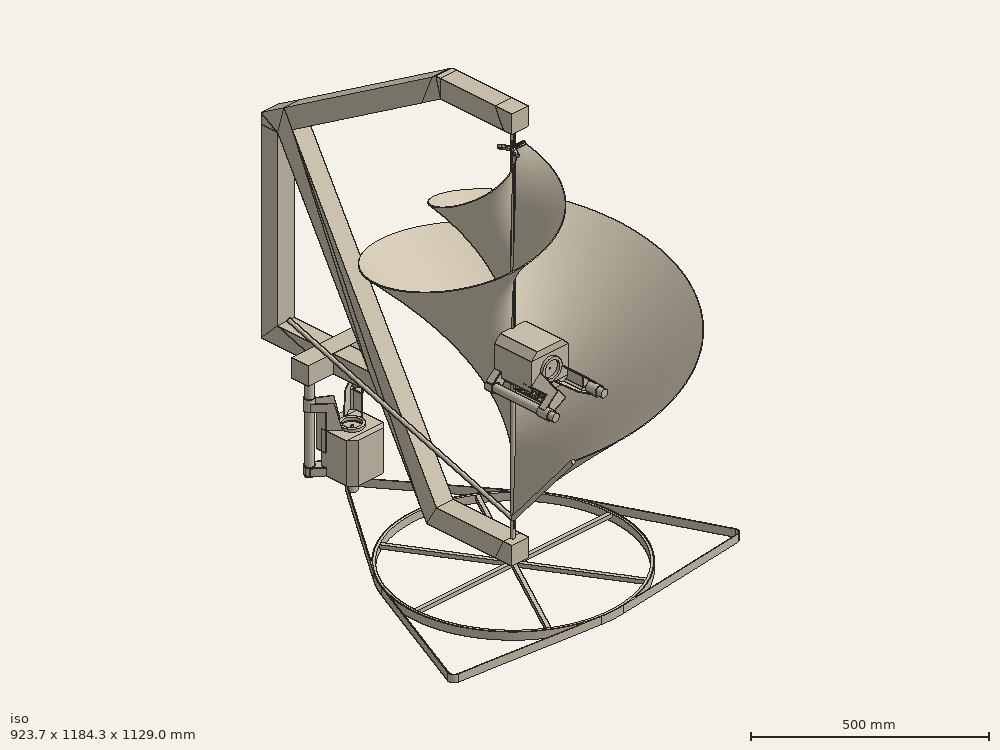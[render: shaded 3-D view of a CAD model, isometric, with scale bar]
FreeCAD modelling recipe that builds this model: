
FCSTD DOCUMENT  (FreeCAD 0.20R29410 (Git))
Label: BASE Con motor
License: All rights reserved
LicenseURL: http://en.wikipedia.org/wiki/All_rights_reserved
objects: Part::Part2DObjectPython×90, Part::Extrusion×53, Part::RuledSurface×40, Sketcher::SketchObject×21, Part::MultiFuse×12, Part::Face×9, Mesh::Feature×9, App::Link×7, Part::FeaturePython×6, App::LinkGroup×5, Part::Feature×5, Part::Cut×4, Part::MultiCommon×4, Part::Cylinder×3, Part::Sweep×2, Part::Helix×1, Part::Offset×1, Part::Fillet×1, App::DocumentObjectGroup×1, Part::Box×1
note: 253 computed .brp shape members not serialized (recipe doc carries the construction recipe); baked Part::Feature solids carry a one-line shape summary decoded from their .brp

FEATURE [Part::Helix] Helix  label="Hélice"
  Angle = -43
  AttacherType = Attacher::AttachEngine3D
  Height = 490
  LocalCoord = 0
  Pitch = 490
  Radius = 490
  SegmentLength = 0
  Style = 1
FEATURE [Sketcher::SketchObject] Sketch001
  ExternalGeometry = -> [Helix]
  FullyConstrained = true
  Placement = pos=(0,0,0) rot=(1,0,0;1.5708rad)
  sketch-geometry (4):
    g0: LineSegment StartX=0 StartY=490 StartZ=0 EndX=0 EndY=-411.159 EndZ=0
    g1: LineSegment StartX=490 StartY=0 StartZ=0 EndX=0 EndY=-411.159 EndZ=0
    g2: LineSegment StartX=490 StartY=0 StartZ=0 EndX=0 EndY=-411.159 EndZ=0
    g3: Circle CenterX=490 CenterY=0 CenterZ=0 NormalX=0 NormalY=0 NormalZ=1 AngleXU=0 Radius=5
  constraints (10):
    c: PointOnObject(g0,g-2)
    c: Horizontal(g0,g-3)
    c: Vertical(g0)
    c: Coincident(g1,g-4)
    c: Coincident(g1,g0)
    c: Angle(g1,g0) = 0.872665
    c: Coincident(g2,g1)
    c: Coincident(g2,g0)
    c: Coincident(g3,g2)
    c: Diameter(g3) = 10
FEATURE [Part::RuledSurface] Ruled_Surface
  Curve1 = -> Sketch001 [Edge1]
  Curve2 = -> Helix [Edge1]
  Orientation = 0
FEATURE [Part::Offset] Offset
  Fill = true
  Intersection = false
  Join = 0
  Mode = 0
  SelfIntersection = false
  Source = -> Ruled_Surface
  Value = 2
FEATURE [Part::Fillet] Fillet
  Base = -> Offset
  Edges = 1 edges r=1: [Edge8]
FEATURE [Sketcher::SketchObject] Sketch
  ExternalGeometry = -> [Helix]
  FullyConstrained = true
  MapMode = 2
  sketch-geometry (2):
    g0: Circle CenterX=0 CenterY=0 CenterZ=0 NormalX=0 NormalY=0 NormalZ=1 AngleXU=0 Radius=5
    g1: LineSegment StartX=33.0676 StartY=0 StartZ=0 EndX=0 EndY=0 EndZ=0
  constraints (4):
    c: Coincident(g0,g-1)
    c: Diameter(g0) = 10
    c: Coincident(g1,g-3)
    c: Coincident(g1,g0)
FEATURE [Sketcher::SketchObject] Sketch002
  ExternalGeometry = -> [Helix]
  FullyConstrained = true
  Placement = pos=(0,0,0) rot=(0.57735,0.57735,0.57735;2.0944rad)
  sketch-geometry (1):
    g0: Circle CenterX=0 CenterY=490 CenterZ=0 NormalX=0 NormalY=0 NormalZ=1 AngleXU=0 Radius=5
  constraints (2):
    c: Coincident(g0,g-3)
    c: Diameter(g0) = 10
FEATURE [Part::Cylinder] Cylinder  label="Cilindro"
  Angle = 360
  AttacherType = Attacher::AttachEngine3D
  FirstAngle = 0
  Height = 640
  Placement = pos=(0,0,-411.16) rot=(0,1,0;0.872665rad)
  Radius = 5
  SecondAngle = 0
FEATURE [Sketcher::SketchObject] Sketch003
  FullyConstrained = true
  sketch-geometry (1):
    g0: Circle CenterX=0 CenterY=0 CenterZ=0 NormalX=0 NormalY=0 NormalZ=1 AngleXU=0 Radius=5
  constraints (2):
    c: Coincident(g0,g-1)
    c: Diameter(g0) = 10
FEATURE [Sketcher::SketchObject] Sketch004
  ExternalGeometry = -> [Helix,Sketch001]
  FullyConstrained = true
  Placement = pos=(0,0,0) rot=(1,0,0;1.5708rad)
  sketch-geometry (1):
    g0: LineSegment StartX=0 StartY=539.42 StartZ=0 EndX=0 EndY=-460.579 EndZ=0
  constraints (4):
    c: Vertical(g0)
    c: DistanceY(g-3,g0) = 49.42
    c: DistanceY(g0,g-4) = 49.42
    c: Vertical(g0,g-4)
FEATURE [Part::Sweep] Sweep
  Frenet = false
  Sections = -> [Sketch003]
  Solid = true
  Spine = -> Sketch004 [Edge1]
  Transition = 1
FEATURE [Part::Sweep] Sweep001
  Frenet = false
  Sections = -> [Sketch002]
  Solid = true
  Spine = -> Sketch [Edge2]
  Transition = 1
FEATURE [Sketcher::SketchObject] Sketch005
  ExternalGeometry = -> [Helix]
  FullyConstrained = true
  Placement = pos=(0,0,0) rot=(1,0,0;1.5708rad)
  sketch-geometry (1):
    g0: Circle CenterX=490 CenterY=0 CenterZ=0 NormalX=0 NormalY=0 NormalZ=1 AngleXU=0 Radius=5
  constraints (2):
    c: Coincident(g0,g-3)
    c: Diameter(g0) = 10
FEATURE [Part::Part2DObjectPython] Line007  # Draft 2D object (typed FeaturePython)
  Area = 0
  ChamferSize = 0
  Closed = false
  End = (3e-14,3855,-1010.3)
  FilletRadius = 0
  Length = 45.7
  MakeFace = true
  Placement = pos=(2.7e-14,3855,-1056) rot=(0.57735,0.57735,0.57735;2.0944rad)
  Points = (2) [(0,0,0),(0,45.7,2.79832e-15)]
  Start = (2.72e-14,3855,-1056)
  Subdivisions = 0
FEATURE [Part::Part2DObjectPython] Line010  # Draft 2D object (typed FeaturePython)
  Area = 0
  ChamferSize = 0
  Closed = false
  End = (8.8e-14,3855,-101.7)
  FilletRadius = 0
  Length = 45.7
  MakeFace = true
  Placement = pos=(8.8e-14,3855,-56) rot=(0.57735,0.57735,0.57735;2.0944rad)
  Points = (2) [(0,0,0),(0,-45.7,0)]
  Start = (8.8e-14,3855,-56)
  Subdivisions = 0
FEATURE [Part::Part2DObjectPython] Line019  # Draft 2D object (typed FeaturePython)
  Area = 0
  ChamferSize = 0
  Closed = false
  End = (5.71e-14,4300,-568.3)
  FilletRadius = 0
  Length = 890
  MakeFace = true
  Placement = pos=(5.7e-14,3410,-568.3) rot=(0.57735,0.57735,0.57735;2.0944rad)
  Points = (2) [(0,0,0),(890,0,0)]
  Start = (5.71e-14,3410,-568.3)
  Subdivisions = 0
FEATURE [Part::Part2DObjectPython] Line020  # Draft 2D object (typed FeaturePython)
  Area = 0
  ChamferSize = 0
  Closed = false
  End = (3e-14,3855,-1010.3)
  FilletRadius = 0
  Length = 627.207
  MakeFace = true
  Placement = pos=(5.7e-14,3410,-568.3) rot=(0.57735,0.57735,0.57735;2.0944rad)
  Points = (2) [(0,0,0),(445,-442,-2.70647e-14)]
  Start = (5.71e-14,3410,-568.3)
  Subdivisions = 0
FEATURE [Part::Part2DObjectPython] Line021  # Draft 2D object (typed FeaturePython)
  Area = 0
  ChamferSize = 0
  Closed = false
  End = (3e-14,3855,-1010.3)
  FilletRadius = 0
  Length = 627.207
  MakeFace = true
  Placement = pos=(5.7e-14,4300,-568.3) rot=(0.57735,0.57735,0.57735;2.0944rad)
  Points = (2) [(0,0,0),(-445,-442,-2.70647e-14)]
  Start = (5.71e-14,4300,-568.3)
  Subdivisions = 0
FEATURE [Part::Part2DObjectPython] Line028  # Draft 2D object (typed FeaturePython)
  Area = 0
  ChamferSize = 0
  Closed = false
  End = (0,4125,-311)
  FilletRadius = 0
  Length = 270
  MakeFace = true
  Placement = pos=(0,3855,-311) rot=(0.57735,0.57735,0.57735;2.0944rad)
  Points = (2) [(0,0,0),(270,0,0)]
  Start = (0,3855,-311)
  Subdivisions = 0
FEATURE [Part::Part2DObjectPython] Line029  # Draft 2D object (typed FeaturePython)
  Area = 0
  ChamferSize = 0
  Closed = false
  End = (0,3585,-311)
  FilletRadius = 0
  Length = 270
  MakeFace = true
  Placement = pos=(0,3855,-311) rot=(0.57735,0.57735,0.57735;2.0944rad)
  Points = (2) [(0,0,0),(-270,0,0)]
  Start = (0,3855,-311)
  Subdivisions = 0
FEATURE [Part::Part2DObjectPython] Line030  # Draft 2D object (typed FeaturePython)
  Area = 0
  ChamferSize = 0
  Closed = false
  End = (5.71e-14,3855,-568.3)
  FilletRadius = 0
  Length = 372.966
  MakeFace = true
  Placement = pos=(0,3585,-311) rot=(0.57735,0.57735,0.57735;2.0944rad)
  Points = (2) [(0,0,0),(270,-257.3,5.71114e-14)]
  Start = (0,3585,-311)
  Subdivisions = 0
FEATURE [Part::Part2DObjectPython] Line031  # Draft 2D object (typed FeaturePython)
  Area = 0
  ChamferSize = 0
  Closed = false
  End = (5.71e-14,3855,-568.3)
  FilletRadius = 0
  Length = 372.966
  MakeFace = true
  Placement = pos=(0,4125,-311) rot=(0.57735,0.57735,0.57735;2.0944rad)
  Points = (2) [(0,0,0),(-270,-257.3,5.71114e-14)]
  Start = (0,4125,-311)
  Subdivisions = 0
FEATURE [Part::Part2DObjectPython] Line032  # Draft 2D object (typed FeaturePython)
  Area = 0
  ChamferSize = 0
  Closed = false
  End = (8.8e-14,3735,-101.7)
  FilletRadius = 0
  Length = 120
  MakeFace = true
  Placement = pos=(8.8e-14,3855,-101.7) rot=(0.57735,0.57735,0.57735;2.0944rad)
  Points = (2) [(0,0,0),(-120,0,0)]
  Start = (8.8e-14,3855,-101.7)
  Subdivisions = 0
FEATURE [Part::Part2DObjectPython] Line033  # Draft 2D object (typed FeaturePython)
  Area = 0
  ChamferSize = 0
  Closed = false
  End = (-5e-16,3855,-311.004)
  FilletRadius = 0
  Length = 241.264
  MakeFace = true
  Placement = pos=(8.8e-14,3735,-101.7) rot=(0.57735,0.57735,0.57735;2.0944rad)
  Points = (2) [(0,0,0),(120.002,-209.304,-8.84807e-14)]
  Start = (8.8e-14,3735,-101.7)
  Subdivisions = 0
FEATURE [Part::Part2DObjectPython] Line034  # Draft 2D object (typed FeaturePython)
  Area = 0
  ChamferSize = 0
  Closed = false
  End = (8.8e-14,3975,-101.7)
  FilletRadius = 0
  Length = 120
  MakeFace = true
  Placement = pos=(8.8e-14,3855,-101.7) rot=(0.57735,0.57735,0.57735;2.0944rad)
  Points = (2) [(0,0,0),(120,0,0)]
  Start = (8.8e-14,3855,-101.7)
  Subdivisions = 0
FEATURE [Part::Part2DObjectPython] Line035  # Draft 2D object (typed FeaturePython)
  Area = 0
  ChamferSize = 0
  Closed = false
  End = (-5e-16,3855,-311)
  FilletRadius = 0
  Length = 241.26
  MakeFace = true
  Placement = pos=(8.8e-14,3975,-101.7) rot=(0.57735,0.57735,0.57735;2.0944rad)
  Points = (2) [(0,0,0),(-120,-209.3,-8.84807e-14)]
  Start = (8.8e-14,3975,-101.7)
  Subdivisions = 0
FEATURE [Part::Part2DObjectPython] Line036  # Draft 2D object (typed FeaturePython)
  Area = 0
  ChamferSize = 0
  Closed = false
  End = (2.72e-14,3915,-1056)
  FilletRadius = 0
  Length = 60
  MakeFace = true
  Placement = pos=(2.7e-14,3855,-1056) rot=(0.57735,0.57735,0.57735;2.0944rad)
  Points = (2) [(0,0,0),(60,0,0)]
  Start = (2.72e-14,3855,-1056)
  Subdivisions = 0
FEATURE [Part::Part2DObjectPython] Line037  # Draft 2D object (typed FeaturePython)
  Area = 0
  ChamferSize = 0
  Closed = false
  End = (2.72e-14,3795,-1056)
  FilletRadius = 0
  Length = 60
  MakeFace = true
  Placement = pos=(2.7e-14,3855,-1056) rot=(0.57735,0.57735,0.57735;2.0944rad)
  Points = (2) [(0,0,0),(-60,0,0)]
  Start = (2.72e-14,3855,-1056)
  Subdivisions = 0
FEATURE [Part::Part2DObjectPython] Line038  # Draft 2D object (typed FeaturePython)
  Area = 0
  ChamferSize = 0
  Closed = false
  End = (2.72e-14,3795,-1176)
  FilletRadius = 0
  Length = 120
  MakeFace = true
  Placement = pos=(2.7e-14,3795,-1056) rot=(0.57735,0.57735,0.57735;2.0944rad)
  Points = (2) [(0,0,0),(0,-120,0)]
  Start = (2.72e-14,3795,-1056)
  Subdivisions = 0
FEATURE [Part::Part2DObjectPython] Line039  # Draft 2D object (typed FeaturePython)
  Area = 0
  ChamferSize = 0
  Closed = false
  End = (2.72e-14,4155,-1176)
  FilletRadius = 0
  Length = 360
  MakeFace = true
  Placement = pos=(2.7e-14,3795,-1176) rot=(0.57735,0.57735,0.57735;2.0944rad)
  Points = (2) [(0,0,0),(360,0,0)]
  Start = (2.72e-14,3795,-1176)
  Subdivisions = 0
FEATURE [Part::Part2DObjectPython] Line040  # Draft 2D object (typed FeaturePython)
  Area = 0
  ChamferSize = 0
  Closed = false
  End = (2.72e-14,4155,-1056)
  FilletRadius = 0
  Length = 240
  MakeFace = true
  Placement = pos=(2.7e-14,3915,-1056) rot=(0.57735,0.57735,0.57735;2.0944rad)
  Points = (2) [(0,0,0),(240,0,0)]
  Start = (2.72e-14,3915,-1056)
  Subdivisions = 0
FEATURE [Part::Part2DObjectPython] Line041  # Draft 2D object (typed FeaturePython)
  Area = 0
  ChamferSize = 0
  Closed = false
  End = (8.8e-14,3795,-56)
  FilletRadius = 0
  Length = 60
  MakeFace = true
  Placement = pos=(8.8e-14,3855,-56) rot=(0.57735,0.57735,0.57735;2.0944rad)
  Points = (2) [(0,0,0),(-60,0,0)]
  Start = (8.8e-14,3855,-56)
  Subdivisions = 0
FEATURE [Part::Part2DObjectPython] Line042  # Draft 2D object (typed FeaturePython)
  Area = 0
  ChamferSize = 0
  Closed = false
  End = (8.8e-14,3795,64)
  FilletRadius = 0
  Length = 120
  MakeFace = true
  Placement = pos=(8.8e-14,3795,-56) rot=(0.57735,0.57735,0.57735;2.0944rad)
  Points = (2) [(0,0,0),(0,120,0)]
  Start = (8.8e-14,3795,-56)
  Subdivisions = 0
FEATURE [Part::Part2DObjectPython] Line043  # Draft 2D object (typed FeaturePython)
  Area = 0
  ChamferSize = 0
  Closed = false
  End = (8.8e-14,3915,64)
  FilletRadius = 0
  Length = 120
  MakeFace = true
  Placement = pos=(8.8e-14,3795,64) rot=(0.57735,0.57735,0.57735;2.0944rad)
  Points = (2) [(0,0,0),(120,0,0)]
  Start = (8.8e-14,3795,64)
  Subdivisions = 0
FEATURE [Part::Part2DObjectPython] Line045  # Draft 2D object (typed FeaturePython)
  Area = 0
  ChamferSize = 0
  Closed = false
  End = (8.8e-14,3855,-56)
  FilletRadius = 0
  Length = 60
  MakeFace = true
  Placement = pos=(8.8e-14,3915,-56) rot=(0.57735,0.57735,0.57735;2.0944rad)
  Points = (2) [(0,0,0),(-60,0,0)]
  Start = (8.8e-14,3915,-56)
  Subdivisions = 0
FEATURE [Part::Part2DObjectPython] Line048  # Draft 2D object (typed FeaturePython)
  Area = 0
  ChamferSize = 0
  Closed = false
  End = (8.8e-14,3855,184)
  FilletRadius = 0
  Length = 15
  MakeFace = true
  Placement = pos=(8.8e-14,3840,184) rot=(0.57735,0.57735,0.57735;2.0944rad)
  Points = (2) [(0,0,0),(15,0,0)]
  Start = (8.8e-14,3840,184)
  Subdivisions = 0
FEATURE [Part::Part2DObjectPython] Line049  # Draft 2D object (typed FeaturePython)
  Area = 0
  ChamferSize = 0
  Closed = false
  End = (8.8e-14,3870,184)
  FilletRadius = 0
  Length = 15
  MakeFace = true
  Placement = pos=(8.8e-14,3855,184) rot=(0.57735,0.57735,0.57735;2.0944rad)
  Points = (2) [(0,0,0),(15,0,0)]
  Start = (8.8e-14,3855,184)
  Subdivisions = 0
FEATURE [Part::Part2DObjectPython] Line052  # Draft 2D object (typed FeaturePython)
  Area = 0
  ChamferSize = 0
  Closed = false
  End = (8.8e-14,3840,184)
  FilletRadius = 0
  Length = 128.16
  MakeFace = true
  Placement = pos=(8.8e-14,3795,64) rot=(0.57735,0.57735,0.57735;2.0944rad)
  Points = (2) [(0,0,0),(45,120,0)]
  Start = (8.8e-14,3795,64)
  Subdivisions = 0
FEATURE [Part::Part2DObjectPython] Line053  # Draft 2D object (typed FeaturePython)
  Area = 0
  ChamferSize = 0
  Closed = false
  End = (8.8e-14,3915,64)
  FilletRadius = 0
  Length = 128.16
  MakeFace = true
  Placement = pos=(8.8e-14,3870,184) rot=(0.57735,0.57735,0.57735;2.0944rad)
  Points = (2) [(0,0,0),(45,-120,0)]
  Start = (8.8e-14,3870,184)
  Subdivisions = 0
FEATURE [Part::Part2DObjectPython] Line056  # Draft 2D object (typed FeaturePython)
  Area = 0
  ChamferSize = 0
  Closed = false
  End = (8.8e-14,4035,-56)
  FilletRadius = 0
  Length = 120
  MakeFace = true
  Placement = pos=(8.8e-14,3915,-56) rot=(0.57735,0.57735,0.57735;2.0944rad)
  Points = (2) [(0,0,0),(120,0,0)]
  Start = (8.8e-14,3915,-56)
  Subdivisions = 0
FEATURE [Part::Part2DObjectPython] Line065  # Draft 2D object (typed FeaturePython)
  Area = 0
  ChamferSize = 0
  Closed = false
  End = (2.72e-14,4239.02,-1176)
  FilletRadius = 0
  Length = 82.7215
  MakeFace = true
  Placement = pos=(2.7e-14,4156.3,-1176) rot=(0.57735,0.57735,0.57735;2.0944rad)
  Points = (2) [(0,0,0),(82.7215,0,0)]
  Start = (2.72e-14,4156.3,-1176)
  Subdivisions = 0
FEATURE [Part::Part2DObjectPython] Line067  # Draft 2D object (typed FeaturePython)
  Area = 0
  ChamferSize = 0
  Closed = false
  End = (8.8e-14,4036.92,64)
  FilletRadius = 0
  Length = 120
  MakeFace = true
  Placement = pos=(8.8e-14,3916.92,64) rot=(0.57735,0.57735,0.57735;2.0944rad)
  Points = (2) [(0,0,0),(120,0,0)]
  Start = (8.8e-14,3916.92,64)
  Subdivisions = 0
FEATURE [Part::Part2DObjectPython] Line074  # Draft 2D object (typed FeaturePython)
  Area = 0
  ChamferSize = 0
  Closed = false
  End = (2.75e-14,4239.02,-1176)
  FilletRadius = 0
  Length = 262.016
  MakeFace = true
  Placement = pos=(5.2e-14,4328.64,-929.785) rot=(0.57735,0.57735,0.57735;2.0944rad)
  Points = (2) [(0,0,0),(-89.6141,-246.215,-2.44929e-14)]
  Start = (5.2e-14,4328.64,-929.785)
  Subdivisions = 0
FEATURE [Part::Part2DObjectPython] Line080  # Draft 2D object (typed FeaturePython)
  Area = 0
  ChamferSize = 0
  Closed = false
  End = (6.12e-14,4478.64,-929.785)
  FilletRadius = 0
  Length = 150
  MakeFace = true
  Placement = pos=(5.2e-14,4328.64,-929.785) rot=(0.57735,0.57735,0.57735;2.0944rad)
  Points = (2) [(0,0,0),(150,0,9.18485e-15)]
  Start = (5.2e-14,4328.64,-929.785)
  Subdivisions = 0
FEATURE [Part::Part2DObjectPython] Line081  # Draft 2D object (typed FeaturePython)
  Area = 0
  ChamferSize = 0
  Closed = false
  End = (6.09e-14,4478.64,-1176)
  FilletRadius = 0
  Length = 246.215
  MakeFace = true
  Placement = pos=(6.1e-14,4478.64,-929.785) rot=(0.57735,0.57735,0.57735;2.0944rad)
  Points = (2) [(0,0,0),(0,-246.215,0)]
  Start = (6.09e-14,4478.64,-929.785)
  Subdivisions = 0
FEATURE [Part::Part2DObjectPython] Line083  # Draft 2D object (typed FeaturePython)
  Area = 0
  ChamferSize = 0
  Closed = false
  End = (6.09e-14,4529.68,-1176)
  FilletRadius = 0
  Length = 51.04
  MakeFace = true
  Placement = pos=(6.1e-14,4478.64,-1176) rot=(0.57735,0.57735,0.57735;2.0944rad)
  Points = (2) [(0,0,0),(51.04,0,0)]
  Start = (6.09e-14,4478.64,-1176)
  Subdivisions = 0
FEATURE [Part::Part2DObjectPython] Line084  # Draft 2D object (typed FeaturePython)
  Area = 0
  ChamferSize = 0
  Closed = false
  End = (6.09e-14,4529.68,-929.785)
  FilletRadius = 0
  Length = 246.215
  MakeFace = true
  Placement = pos=(6.1e-14,4529.68,-1176) rot=(0.57735,0.57735,0.57735;2.0944rad)
  Points = (2) [(0,0,0),(0,246.215,0)]
  Start = (6.09e-14,4529.68,-1176)
  Subdivisions = 0
FEATURE [Part::Part2DObjectPython] Line085  # Draft 2D object (typed FeaturePython)
  Area = 0
  ChamferSize = 0
  Closed = false
  End = (7.01e-14,4679.68,-929.785)
  FilletRadius = 0
  Length = 150
  MakeFace = true
  Placement = pos=(6.1e-14,4529.68,-929.785) rot=(0.57735,0.57735,0.57735;2.0944rad)
  Points = (2) [(0,0,0),(150,0,9.18485e-15)]
  Start = (6.09e-14,4529.68,-929.785)
  Subdivisions = 0
FEATURE [Part::Part2DObjectPython] Line086  # Draft 2D object (typed FeaturePython)
  Area = 0
  ChamferSize = 0
  Closed = false
  End = (7.01e-14,4679.68,-570.81)
  FilletRadius = 0
  Length = 358.975
  MakeFace = true
  Placement = pos=(7e-14,4679.68,-929.785) rot=(0.57735,0.57735,0.57735;2.0944rad)
  Points = (2) [(0,0,0),(0,358.975,0)]
  Start = (7.01e-14,4679.68,-929.785)
  Subdivisions = 0
FEATURE [Part::Part2DObjectPython] Line088  # Draft 2D object (typed FeaturePython)
  Area = 0
  ChamferSize = 0
  Closed = false
  End = (5.2e-14,4559.68,-817.025)
  FilletRadius = 0
  Length = 190
  MakeFace = true
  Placement = pos=(5.2e-14,4369.68,-817.025) rot=(0.57735,0.57735,0.57735;2.0944rad)
  Points = (2) [(0,0,0),(190,0,0)]
  Start = (5.2e-14,4369.68,-817.025)
  Subdivisions = 0
FEATURE [Part::Part2DObjectPython] Line091  # Draft 2D object (typed FeaturePython)
  Area = 0
  ChamferSize = 0
  Closed = false
  End = (7.01e-14,4679.68,-450.81)
  FilletRadius = 0
  Length = 120
  MakeFace = true
  Placement = pos=(7e-14,4679.68,-570.81) rot=(0.57735,0.57735,0.57735;2.0944rad)
  Points = (2) [(0,0,0),(0,120,0)]
  Start = (7.01e-14,4679.68,-570.81)
  Subdivisions = 0
FEATURE [Part::Part2DObjectPython] Line096  # Draft 2D object (typed FeaturePython)
  Area = 0
  ChamferSize = 0
  Closed = false
  End = (8.8e-14,4066.16,64)
  FilletRadius = 0
  Length = 29.2349
  MakeFace = true
  Placement = pos=(8.8e-14,4036.92,64) rot=(0.57735,0.57735,0.57735;2.0944rad)
  Points = (2) [(0,0,0),(29.2349,0,0)]
  Start = (8.8e-14,4036.92,64)
  Subdivisions = 0
FEATURE [Part::Part2DObjectPython] Line101  # Draft 2D object (typed FeaturePython)
  Area = 0
  ChamferSize = 0
  Closed = false
  End = (7.01e-14,4679.68,-304.25)
  FilletRadius = 0
  Length = 146.56
  MakeFace = true
  Placement = pos=(7e-14,4679.68,-450.81) rot=(0.57735,0.57735,0.57735;2.0944rad)
  Points = (2) [(0,0,0),(0,146.56,0)]
  Start = (7.01e-14,4679.68,-450.81)
  Subdivisions = 0
FEATURE [Part::Part2DObjectPython] Line102  # Draft 2D object (typed FeaturePython)
  Area = 0
  ChamferSize = 0
  Closed = false
  End = (7.75e-14,4437.17,-280.75)
  FilletRadius = 0
  Length = 825.005
  MakeFace = true
  Placement = pos=(2.7e-14,4155,-1056) rot=(0.57735,0.57735,0.57735;2.0944rad)
  Points = (2) [(0,0,0),(282.17,775.25,5.05167e-14)]
  Start = (2.72e-14,4155,-1056)
  Subdivisions = 0
FEATURE [Part::Part2DObjectPython] Line103  # Draft 2D object (typed FeaturePython)
  Area = 0
  ChamferSize = 0
  Closed = false
  End = (7.73e-14,4437.17,-280.75)
  FilletRadius = 0
  Length = 460.71
  MakeFace = true
  Placement = pos=(8.8e-14,4035,-56) rot=(0.57735,0.57735,0.57735;2.0944rad)
  Points = (2) [(0,0,0),(402.17,-224.75,-1.07157e-14)]
  Start = (8.8e-14,4035,-56)
  Subdivisions = 0
FEATURE [Part::Part2DObjectPython] Line106  # Draft 2D object (typed FeaturePython)
  Area = 0
  ChamferSize = 0
  Closed = false
  End = (8.51e-14,4495.71,-176)
  FilletRadius = 0
  Length = 460.71
  MakeFace = true
  Placement = pos=(9.6e-14,4093.54,48.75) rot=(0.57735,0.57735,0.57735;2.0944rad)
  Points = (2) [(0,0,0),(402.17,-224.75,-1.07157e-14)]
  Start = (9.58e-14,4093.54,48.75)
  Subdivisions = 0
FEATURE [Part::Part2DObjectPython] Line107  # Draft 2D object (typed FeaturePython)
  Area = 0
  ChamferSize = 0
  Closed = false
  End = (9.66e-14,4066.25,64)
  FilletRadius = 0
  Length = 31.2606
  MakeFace = true
  Placement = pos=(9.6e-14,4093.54,48.75) rot=(0.57735,0.57735,0.57735;2.0944rad)
  Points = (2) [(0,0,0),(-27.2885,15.25,7.27091e-16)]
  Start = (9.58e-14,4093.54,48.75)
  Subdivisions = 0
FEATURE [Part::Part2DObjectPython] Line108  # Draft 2D object (typed FeaturePython)
  Area = 0
  ChamferSize = 0
  Closed = false
  End = (7.01e-14,4679.68,-278.808)
  FilletRadius = 0
  Length = 210.744
  MakeFace = true
  Placement = pos=(8.5e-14,4495.71,-176) rot=(0.57735,0.57735,0.57735;2.0944rad)
  Points = (2) [(0,0,0),(183.966,-102.808,-1.50019e-14)]
  Start = (8.51e-14,4495.71,-176)
  Subdivisions = 0
FEATURE [Part::Part2DObjectPython] Line109  # Draft 2D object (typed FeaturePython)
  Area = 0
  ChamferSize = 0
  Closed = false
  End = (7.01e-14,4679.68,-278.808)
  FilletRadius = 0
  Length = 25.4419
  MakeFace = true
  Placement = pos=(7e-14,4679.68,-304.25) rot=(0.57735,0.57735,0.57735;2.0944rad)
  Points = (2) [(0,0,0),(0,25.4419,0)]
  Start = (7.01e-14,4679.68,-304.25)
  Subdivisions = 0
FEATURE [Part::Part2DObjectPython] Line112  # Draft 2D object (typed FeaturePython)
  Area = 0
  ChamferSize = 0
  Closed = false
  End = (7.48e-14,4559.68,-349.212)
  FilletRadius = 0
  Length = 467.813
  MakeFace = true
  Placement = pos=(5.2e-14,4559.68,-817.025) rot=(0.57735,0.57735,0.57735;2.0944rad)
  Points = (2) [(0,0,0),(0,467.813,2.27596e-14)]
  Start = (5.2e-14,4559.68,-817.025)
  Subdivisions = 0
FEATURE [Part::Part2DObjectPython] Line113  # Draft 2D object (typed FeaturePython)
  Area = 0
  ChamferSize = 0
  Closed = false
  End = (8.31e-14,4543.28,-340.047)
  FilletRadius = 0
  Length = 507.589
  MakeFace = true
  Placement = pos=(5.2e-14,4369.68,-817.025) rot=(0.57735,0.57735,0.57735;2.0944rad)
  Points = (2) [(0,0,0),(173.606,476.978,3.10809e-14)]
  Start = (5.2e-14,4369.68,-817.025)
  Subdivisions = 0
FEATURE [Part::Part2DObjectPython] Line114  # Draft 2D object (typed FeaturePython)
  Area = 0
  ChamferSize = 0
  Closed = false
  End = (7.62e-14,4543.37,-339.799)
  FilletRadius = 0
  Length = 18.826
  MakeFace = true
  Placement = pos=(7.5e-14,4559.68,-349.212) rot=(0.57735,0.57735,0.57735;2.0944rad)
  Points = (2) [(0,0,0),(-16.3038,9.413,1.15276e-15)]
  Start = (7.5e-14,4559.68,-349.212)
  Subdivisions = 0
FEATURE [Part::Part2DObjectPython] Line115  # Draft 2D object (typed FeaturePython)
  Area = 0
  ChamferSize = 0
  Closed = false
  End = (7.57e-14,4543.37,-339.799)
  FilletRadius = 0
  Length = 0.264679
  MakeFace = true
  Placement = pos=(8.3e-14,4543.28,-340.047) rot=(0.57735,0.57735,0.57735;2.0944rad)
  Points = (2) [(0,0,0),(0.0905213,0.248718,-7.16848e-15)]
  Start = (8.28e-14,4543.28,-340.047)
  Subdivisions = 0
FEATURE [Part::Part2DObjectPython] Line022  # Draft 2D object (typed FeaturePython)
  Area = 0
  ChamferSize = 0
  Closed = false
  End = (3e-14,3855,-101.7)
  FilletRadius = 0
  Length = 908.6
  MakeFace = true
  Placement = pos=(3e-14,3855,-1010.3) rot=(0.57735,0.57735,0.57735;2.0944rad)
  Points = (2) [(0,0,0),(0,908.6,0)]
  Start = (3e-14,3855,-1010.3)
  Subdivisions = 0
FEATURE [Part::Part2DObjectPython] Line116  # Draft 2D object (typed FeaturePython)
  Area = 0
  ChamferSize = 0
  Closed = false
  End = (3e-14,3855,-1010.3)
  FilletRadius = 0
  Length = 627.207
  MakeFace = true
  Placement = pos=(5.7e-14,3410,-568.3) rot=(0.57735,0.57735,0.57735;2.0944rad)
  Points = (2) [(0,0,0),(445,-442,-2.70647e-14)]
  Start = (5.71e-14,3410,-568.3)
  Subdivisions = 0
FEATURE [Part::Part2DObjectPython] Line117  # Draft 2D object (typed FeaturePython)
  Area = 0
  ChamferSize = 0
  Closed = false
  End = (3e-14,3855,-1010.3)
  FilletRadius = 0
  Length = 45.7
  MakeFace = true
  Placement = pos=(2.7e-14,3855,-1056) rot=(0.57735,0.57735,0.57735;2.0944rad)
  Points = (2) [(0,0,0),(0,45.7,2.79832e-15)]
  Start = (2.72e-14,3855,-1056)
  Subdivisions = 0
FEATURE [Part::Part2DObjectPython] Line118  # Draft 2D object (typed FeaturePython)
  Area = 0
  ChamferSize = 0
  Closed = false
  End = (3e-14,3855,-101.7)
  FilletRadius = 0
  Length = 908.6
  MakeFace = true
  Placement = pos=(3e-14,3855,-1010.3) rot=(0.57735,0.57735,0.57735;2.0944rad)
  Points = (2) [(0,0,0),(0,908.6,0)]
  Start = (3e-14,3855,-1010.3)
  Subdivisions = 0
FEATURE [Part::Part2DObjectPython] Line119  # Draft 2D object (typed FeaturePython)
  Area = 0
  ChamferSize = 0
  Closed = false
  End = (3e-14,3855,-1010.3)
  FilletRadius = 0
  Length = 627.207
  MakeFace = true
  Placement = pos=(5.7e-14,4300,-568.3) rot=(0.57735,0.57735,0.57735;2.0944rad)
  Points = (2) [(0,0,0),(-445,-442,-2.70647e-14)]
  Start = (5.71e-14,4300,-568.3)
  Subdivisions = 0
FEATURE [Part::Part2DObjectPython] Line120  # Draft 2D object (typed FeaturePython)
  Area = 0
  ChamferSize = 0
  Closed = false
  End = (5.71e-14,4300,-568.3)
  FilletRadius = 0
  Length = 890
  MakeFace = true
  Placement = pos=(5.7e-14,3410,-568.3) rot=(0.57735,0.57735,0.57735;2.0944rad)
  Points = (2) [(0,0,0),(890,0,0)]
  Start = (5.71e-14,3410,-568.3)
  Subdivisions = 0
FEATURE [Part::Part2DObjectPython] Line121  # Draft 2D object (typed FeaturePython)
  Area = 0
  ChamferSize = 0
  Closed = false
  End = (5.71e-14,3855,-568.3)
  FilletRadius = 0
  Length = 372.966
  MakeFace = true
  Placement = pos=(0,3585,-311) rot=(0.57735,0.57735,0.57735;2.0944rad)
  Points = (2) [(0,0,0),(270,-257.3,5.71114e-14)]
  Start = (0,3585,-311)
  Subdivisions = 0
FEATURE [Part::Part2DObjectPython] Line122  # Draft 2D object (typed FeaturePython)
  Area = 0
  ChamferSize = 0
  Closed = false
  End = (5.71e-14,3855,-568.3)
  FilletRadius = 0
  Length = 372.966
  MakeFace = true
  Placement = pos=(0,4125,-311) rot=(0.57735,0.57735,0.57735;2.0944rad)
  Points = (2) [(0,0,0),(-270,-257.3,5.71114e-14)]
  Start = (0,4125,-311)
  Subdivisions = 0
FEATURE [Part::Part2DObjectPython] Line123  # Draft 2D object (typed FeaturePython)
  Area = 0
  ChamferSize = 0
  Closed = false
  End = (0,4125,-311)
  FilletRadius = 0
  Length = 270
  MakeFace = true
  Placement = pos=(0,3855,-311) rot=(0.57735,0.57735,0.57735;2.0944rad)
  Points = (2) [(0,0,0),(270,0,0)]
  Start = (0,3855,-311)
  Subdivisions = 0
FEATURE [Part::Part2DObjectPython] Line124  # Draft 2D object (typed FeaturePython)
  Area = 0
  ChamferSize = 0
  Closed = false
  End = (0,3585,-311)
  FilletRadius = 0
  Length = 270
  MakeFace = true
  Placement = pos=(0,3855,-311) rot=(0.57735,0.57735,0.57735;2.0944rad)
  Points = (2) [(0,0,0),(-270,0,0)]
  Start = (0,3855,-311)
  Subdivisions = 0
FEATURE [Part::Part2DObjectPython] Line125  # Draft 2D object (typed FeaturePython)
  Area = 0
  ChamferSize = 0
  Closed = false
  End = (-5e-16,3855,-311.004)
  FilletRadius = 0
  Length = 241.264
  MakeFace = true
  Placement = pos=(8.8e-14,3735,-101.7) rot=(0.57735,0.57735,0.57735;2.0944rad)
  Points = (2) [(0,0,0),(120.002,-209.304,-8.84807e-14)]
  Start = (8.8e-14,3735,-101.7)
  Subdivisions = 0
FEATURE [Part::Part2DObjectPython] Line126  # Draft 2D object (typed FeaturePython)
  Area = 0
  ChamferSize = 0
  Closed = false
  End = (-5e-16,3855,-311)
  FilletRadius = 0
  Length = 241.26
  MakeFace = true
  Placement = pos=(8.8e-14,3975,-101.7) rot=(0.57735,0.57735,0.57735;2.0944rad)
  Points = (2) [(0,0,0),(-120,-209.3,-8.84807e-14)]
  Start = (8.8e-14,3975,-101.7)
  Subdivisions = 0
FEATURE [Part::Part2DObjectPython] Line127  # Draft 2D object (typed FeaturePython)
  Area = 0
  ChamferSize = 0
  Closed = false
  End = (8.8e-14,3735,-101.7)
  FilletRadius = 0
  Length = 120
  MakeFace = true
  Placement = pos=(8.8e-14,3855,-101.7) rot=(0.57735,0.57735,0.57735;2.0944rad)
  Points = (2) [(0,0,0),(-120,0,0)]
  Start = (8.8e-14,3855,-101.7)
  Subdivisions = 0
FEATURE [Part::Part2DObjectPython] Line128  # Draft 2D object (typed FeaturePython)
  Area = 0
  ChamferSize = 0
  Closed = false
  End = (8.8e-14,3975,-101.7)
  FilletRadius = 0
  Length = 120
  MakeFace = true
  Placement = pos=(8.8e-14,3855,-101.7) rot=(0.57735,0.57735,0.57735;2.0944rad)
  Points = (2) [(0,0,0),(120,0,0)]
  Start = (8.8e-14,3855,-101.7)
  Subdivisions = 0
FEATURE [Part::Part2DObjectPython] Line129  # Draft 2D object (typed FeaturePython)
  Area = 0
  ChamferSize = 0
  Closed = false
  End = (8.8e-14,3855,-101.7)
  FilletRadius = 0
  Length = 45.7
  MakeFace = true
  Placement = pos=(8.8e-14,3855,-56) rot=(0.57735,0.57735,0.57735;2.0944rad)
  Points = (2) [(0,0,0),(0,-45.7,0)]
  Start = (8.8e-14,3855,-56)
  Subdivisions = 0
FEATURE [Part::MultiFuse] Fusion
  Placement = pos=(0,-3814,2858) rot=(0,0,1;0rad)
  Shapes = -> [Line129,Line128,Line127,Line126,Line125,Line124,Line123,Line122,Line121,Line120,Line119,Line118,Line117,Line116]
FEATURE [Part::Part2DObjectPython] Line  # Draft 2D object (typed FeaturePython)
  Area = 0
  ChamferSize = 0
  Closed = false
  End = (2.85e-14,16,1802)
  FilletRadius = 0
  Length = 25
  MakeFace = true
  Placement = pos=(2.7e-14,41,1802) rot=(0.57735,0.57735,0.57735;2.0944rad)
  Points = (2) [(0,0,0),(-25,0,1.53081e-15)]
  Start = (2.7e-14,41,1802)
  Subdivisions = 0
FEATURE [Part::Part2DObjectPython] Line130  # Draft 2D object (typed FeaturePython)
  Area = 0
  ChamferSize = 0
  Closed = false
  End = (3.21e-14,16,1752)
  FilletRadius = 0
  Length = 50
  MakeFace = true
  Placement = pos=(2.9e-14,16,1802) rot=(0.57735,0.57735,0.57735;2.0944rad)
  Points = (2) [(0,0,0),(3.55271e-15,-50,3.06162e-15)]
  Start = (2.9e-14,16,1802)
  Subdivisions = 0
FEATURE [Part::Part2DObjectPython] Line131  # Draft 2D object (typed FeaturePython)
  Area = 0
  ChamferSize = 0
  Closed = false
  End = (3.51e-14,66,1752)
  FilletRadius = 0
  Length = 50
  MakeFace = true
  Placement = pos=(3.2e-14,16,1752) rot=(0.57735,0.57735,0.57735;2.0944rad)
  Points = (2) [(0,0,0),(50,0,3.06162e-15)]
  Start = (3.2e-14,16,1752)
  Subdivisions = 0
FEATURE [Part::Part2DObjectPython] Line132  # Draft 2D object (typed FeaturePython)
  Area = 0
  ChamferSize = 0
  Closed = false
  End = (3.92e-14,241,1802)
  FilletRadius = 0
  Length = 200
  MakeFace = true
  Placement = pos=(2.7e-14,41,1802) rot=(0.57735,0.57735,0.57735;2.0944rad)
  Points = (2) [(0,0,0),(200,0,1.22465e-14)]
  Start = (2.7e-14,41,1802)
  Subdivisions = 0
FEATURE [Part::Part2DObjectPython] Line146  # Draft 2D object (typed FeaturePython)
  Area = 0
  ChamferSize = 0
  Closed = false
  End = (8.95e-14,16,2802)
  FilletRadius = 0
  Length = 25
  MakeFace = true
  Placement = pos=(8.8e-14,41,2802) rot=(0.57735,0.57735,0.57735;2.0944rad)
  Points = (2) [(0,0,0),(-25,0,1.53081e-15)]
  Start = (8.8e-14,41,2802)
  Subdivisions = 0
FEATURE [Part::Part2DObjectPython] Line147  # Draft 2D object (typed FeaturePython)
  Area = 0
  ChamferSize = 0
  Closed = false
  End = (9.31e-14,16,2852)
  FilletRadius = 0
  Length = 50
  MakeFace = true
  Placement = pos=(9e-14,16,2802) rot=(0.57735,0.57735,0.57735;2.0944rad)
  Points = (2) [(0,0,0),(3.55271e-15,50,3.06162e-15)]
  Start = (9e-14,16,2802)
  Subdivisions = 0
FEATURE [Part::Part2DObjectPython] Line148  # Draft 2D object (typed FeaturePython)
  Area = 0
  ChamferSize = 0
  Closed = false
  End = (9.61e-14,66,2852)
  FilletRadius = 0
  Length = 50
  MakeFace = true
  Placement = pos=(9.3e-14,16,2852) rot=(0.57735,0.57735,0.57735;2.0944rad)
  Points = (2) [(0,0,0),(50,0,3.06162e-15)]
  Start = (9.3e-14,16,2852)
  Subdivisions = 0
FEATURE [Part::Part2DObjectPython] Line150  # Draft 2D object (typed FeaturePython)
  Area = 0
  ChamferSize = 0
  Closed = false
  End = (8.03e-14,284.583,2769.99)
  FilletRadius = 0
  Length = 446.092
  MakeFace = true
  Placement = pos=(5.3e-14,670.913,2546.95) rot=(0.57735,0.57735,0.57735;2.0944rad)
  Points = (2) [(0,0,0),(-386.33,223.04,2.73151e-14)]
  Start = (5.3e-14,670.913,2546.95)
  Subdivisions = 0
FEATURE [Part::Part2DObjectPython] Line152  # Draft 2D object (typed FeaturePython)
  Area = 0
  ChamferSize = 0
  Closed = false
  End = (8e-14,284.583,2769.99)
  FilletRadius = 0
  Length = 64.026
  MakeFace = true
  Placement = pos=(8.4e-14,229.135,2802) rot=(0.57735,0.57735,0.57735;2.0944rad)
  Points = (2) [(0,0,0),(55.4486,-32.0122,-3.92045e-15)]
  Start = (8.39e-14,229.135,2802)
  Subdivisions = 0
FEATURE [Part::Part2DObjectPython] Line153  # Draft 2D object (typed FeaturePython)
  Area = 0
  ChamferSize = 0
  Closed = false
  End = (8.39e-14,229.135,2802)
  FilletRadius = 0
  Length = 188.135
  MakeFace = true
  Placement = pos=(8.8e-14,41,2802) rot=(0.57735,0.57735,0.57735;2.0944rad)
  Points = (2) [(0,0,0),(188.135,0,-4.10461e-15)]
  Start = (8.8e-14,41,2802)
  Subdivisions = 0
FEATURE [Part::Part2DObjectPython] Line155  # Draft 2D object (typed FeaturePython)
  Area = 0
  ChamferSize = 0
  Closed = false
  End = (5.24e-14,670.913,2546.95)
  FilletRadius = 0
  Length = 860.1
  MakeFace = true
  Placement = pos=(3.9e-14,241,1802) rot=(0.57735,0.57735,0.57735;2.0944rad)
  Points = (2) [(0,0,0),(429.913,744.948,1.34133e-14)]
  Start = (3.92e-14,241,1802)
  Subdivisions = 0
FEATURE [Part::Part2DObjectPython] Line163  # Draft 2D object (typed FeaturePython)
  Area = 0
  ChamferSize = 0
  Closed = false
  End = (9.6e-14,229.135,2852)
  FilletRadius = 0
  Length = 163.135
  MakeFace = true
  Placement = pos=(9.6e-14,66,2852) rot=(0.57735,0.57735,0.57735;2.0944rad)
  Points = (2) [(0,0,0),(163.135,0,0)]
  Start = (9.6e-14,66,2852)
  Subdivisions = 0
FEATURE [Part::Part2DObjectPython] Line167  # Draft 2D object (typed FeaturePython)
  Area = 0
  ChamferSize = 0
  Closed = false
  End = (8.72e-14,254.135,2845.3)
  FilletRadius = 0
  Length = 510.118
  MakeFace = true
  Placement = pos=(5.6e-14,695.913,2590.25) rot=(0.57735,0.57735,0.57735;2.0944rad)
  Points = (2) [(0,0,0),(-441.779,255.052,3.12356e-14)]
  Start = (5.6e-14,695.913,2590.25)
  Subdivisions = 0
FEATURE [Part::Part2DObjectPython] Line168  # Draft 2D object (typed FeaturePython)
  Area = 0
  ChamferSize = 0
  Closed = false
  End = (9.6e-14,242.53,2852)
  FilletRadius = 0
  Length = 13.3949
  MakeFace = true
  Placement = pos=(9.6e-14,229.135,2852) rot=(0.57735,0.57735,0.57735;2.0944rad)
  Points = (2) [(0,0,0),(13.3949,0,0)]
  Start = (9.6e-14,229.135,2852)
  Subdivisions = 0
FEATURE [Part::Part2DObjectPython] Line169  # Draft 2D object (typed FeaturePython)
  Area = 0
  ChamferSize = 0
  Closed = false
  End = (9.57e-14,242.53,2852)
  FilletRadius = 0
  Length = 13.4003
  MakeFace = true
  Placement = pos=(8.7e-14,254.135,2845.3) rot=(0.57735,0.57735,0.57735;2.0944rad)
  Points = (2) [(0,0,0),(-11.6051,6.7,8.69703e-15)]
  Start = (8.7e-14,254.135,2845.3)
  Subdivisions = 0
FEATURE [Part::Part2DObjectPython] Line170  # Draft 2D object (typed FeaturePython)
  Area = 0
  ChamferSize = 0
  Closed = false
  End = (5.88e-14,764.213,2550.82)
  FilletRadius = 0
  Length = 28.8683
  MakeFace = true
  Placement = pos=(5.9e-14,764.213,2521.95) rot=(0.57735,0.57735,0.57735;2.0944rad)
  Points = (2) [(0,0,0),(0,28.8683,0)]
  Start = (5.88e-14,764.213,2521.95)
  Subdivisions = 0
FEATURE [Part::Part2DObjectPython] Line171  # Draft 2D object (typed FeaturePython)
  Area = 0
  ChamferSize = 0
  Closed = false
  End = (5.59e-14,695.913,2590.25)
  FilletRadius = 0
  Length = 78.8654
  MakeFace = true
  Placement = pos=(5.9e-14,764.213,2550.82) rot=(0.57735,0.57735,0.57735;2.0944rad)
  Points = (2) [(0,0,0),(-68.3,39.4317,-3.06162e-15)]
  Start = (5.88e-14,764.213,2550.82)
  Subdivisions = 0
FEATURE [Part::Part2DObjectPython] Line175  # Draft 2D object (typed FeaturePython)
  Area = 0
  ChamferSize = 0
  Closed = false
  End = (3.5e-14,269.872,1752)
  FilletRadius = 0
  Length = 203.872
  MakeFace = true
  Placement = pos=(3.5e-14,66,1752) rot=(0.57735,0.57735,0.57735;2.0944rad)
  Points = (2) [(0,0,0),(203.872,0,0)]
  Start = (3.5e-14,66,1752)
  Subdivisions = 0
FEATURE [Part::Part2DObjectPython] Line176  # Draft 2D object (typed FeaturePython)
  Area = 0
  ChamferSize = 0
  Closed = false
  End = (4.27e-14,284.3,1777)
  FilletRadius = 0
  Length = 28.8645
  MakeFace = true
  Placement = pos=(3.5e-14,269.872,1752) rot=(0.57735,0.57735,0.57735;2.0944rad)
  Points = (2) [(0,0,0),(14.4276,25,7.65404e-15)]
  Start = (3.5e-14,269.872,1752)
  Subdivisions = 0
FEATURE [Part::Part2DObjectPython] Line183  # Draft 2D object (typed FeaturePython)
  Area = 0
  ChamferSize = 0
  Closed = false
  End = (5.3e-14,764.213,2521.95)
  FilletRadius = 0
  Length = 519.948
  MakeFace = true
  Placement = pos=(5.3e-14,764.213,2002) rot=(0.57735,0.57735,0.57735;2.0944rad)
  Points = (2) [(0,0,0),(0,519.948,0)]
  Start = (5.3e-14,764.213,2002)
  Subdivisions = 0
FEATURE [Part::Part2DObjectPython] Line186  # Draft 2D object (typed FeaturePython)
  Area = 0
  ChamferSize = 0
  Closed = false
  End = (5e-14,443.004,2052)
  FilletRadius = 0
  Length = 271.209
  MakeFace = true
  Placement = pos=(5e-14,714.213,2052) rot=(0.57735,0.57735,0.57735;2.0944rad)
  Points = (2) [(0,0,0),(-271.209,0,0)]
  Start = (5e-14,714.213,2052)
  Subdivisions = 0
FEATURE [Part::Part2DObjectPython] Line188  # Draft 2D object (typed FeaturePython)
  Area = 0
  ChamferSize = 0
  Closed = false
  End = (5e-14,714.213,2521.95)
  FilletRadius = 0
  Length = 469.948
  MakeFace = true
  Placement = pos=(5e-14,714.213,2052) rot=(0.57735,0.57735,0.57735;2.0944rad)
  Points = (2) [(0,0,0),(0,469.948,0)]
  Start = (5e-14,714.213,2052)
  Subdivisions = 0
FEATURE [Part::Part2DObjectPython] Line189  # Draft 2D object (typed FeaturePython)
  Area = 0
  ChamferSize = 0
  Closed = false
  End = (5.52e-14,564.301,2002.26)
  FilletRadius = 0
  Length = 150
  MakeFace = true
  Placement = pos=(4.6e-14,414.301,2002.26) rot=(0.57735,0.57735,0.57735;2.0944rad)
  Points = (2) [(0,0,0),(150,0,9.18485e-15)]
  Start = (4.6e-14,414.301,2002.26)
  Subdivisions = 0
FEATURE [Part::Part2DObjectPython] Line193  # Draft 2D object (typed FeaturePython)
  Area = 0
  ChamferSize = 0
  Closed = false
  End = (7.39e-14,764.213,2002.26)
  FilletRadius = 0
  Length = 149.912
  MakeFace = true
  Placement = pos=(7.4e-14,614.301,2002.26) rot=(0.57735,0.57735,0.57735;2.0944rad)
  Points = (2) [(0,0,0),(149.912,0,0)]
  Start = (7.39e-14,614.301,2002.26)
  Subdivisions = 0
FEATURE [Part::Part2DObjectPython] Line195  # Draft 2D object (typed FeaturePython)
  Area = 0
  ChamferSize = 0
  Closed = false
  End = (5.57e-14,714.213,2521.95)
  FilletRadius = 0
  Length = 542.591
  MakeFace = true
  Placement = pos=(5e-14,443.004,2052) rot=(0.57735,0.57735,0.57735;2.0944rad)
  Points = (2) [(0,0,0),(271.209,469.948,5.7593e-15)]
  Start = (5e-14,443.004,2052)
  Subdivisions = 0
FEATURE [Sketcher::SketchObject] Sketch006
  FullyConstrained = true
FEATURE [Part::RuledSurface] Ruled_Surface001
  Curve1 = -> Line131 [Edge1]
  Curve2 = -> Line [Edge1]
  Orientation = 0
FEATURE [Part::RuledSurface] Ruled_Surface002
  Curve1 = -> Line132 [Edge1]
  Curve2 = -> Line175 [Edge1]
  Orientation = 0
FEATURE [Part::RuledSurface] Ruled_Surface003
  Curve1 = -> Line176 [Edge1]
  Curve2 = -> Line155 [Edge1]
  Orientation = 0
FEATURE [Part::RuledSurface] Ruled_Surface005
  Curve1 = -> Line189 [Edge1]
  Curve2 = -> Line186 [Edge1]
  Orientation = 0
FEATURE [Part::RuledSurface] Ruled_Surface006
  Curve1 = -> Line193 [Edge1]
  Curve2 = -> Ruled_Surface005 [Edge2]
  Orientation = 0
FEATURE [Part::RuledSurface] Ruled_Surface007
  Curve1 = -> Line188 [Edge1]
  Curve2 = -> Line183 [Edge1]
  Orientation = 0
FEATURE [Part::RuledSurface] Ruled_Surface008
  Curve1 = -> Line170 [Edge1]
  Curve2 = -> Ruled_Surface007 [Edge2]
  Orientation = 0
FEATURE [Part::RuledSurface] Ruled_Surface009
  Curve1 = -> Ruled_Surface008 [Edge2]
  Curve2 = -> Line171 [Edge1]
  Orientation = 0
FEATURE [Part::RuledSurface] Ruled_Surface010
  Curve1 = -> Line150 [Edge1]
  Curve2 = -> Line167 [Edge1]
  Orientation = 0
FEATURE [Part::RuledSurface] Ruled_Surface011
  Curve1 = -> Ruled_Surface010 [Edge4]
  Curve2 = -> Line195 [Edge1]
  Orientation = 0
FEATURE [Part::RuledSurface] Ruled_Surface012
  Curve1 = -> Ruled_Surface003 [Edge2]
  Curve2 = -> Ruled_Surface011 [Edge2]
  Orientation = 0
FEATURE [Part::RuledSurface] Ruled_Surface013
  Curve1 = -> Line152 [Edge1]
  Curve2 = -> Line169 [Edge1]
  Orientation = 0
FEATURE [Part::RuledSurface] Ruled_Surface014
  Curve1 = -> Line163 [Edge1]
  Curve2 = -> Line153 [Edge1]
  Orientation = 0
FEATURE [Part::RuledSurface] Ruled_Surface015
  Curve1 = -> Ruled_Surface014 [Edge2]
  Curve2 = -> Ruled_Surface013 [Edge4]
  Orientation = 0
FEATURE [Part::RuledSurface] Ruled_Surface016
  Curve1 = -> Line147 [Edge1]
  Curve2 = -> Ruled_Surface014 [Edge4]
  Orientation = 0
FEATURE [Part::Extrusion] Extrude
  Base = -> Ruled_Surface001
  Dir = (1,0,0)
  DirMode = 0
  FaceMakerClass = Part::FaceMakerBullseye
  LengthFwd = 50
  LengthRev = 0
  Solid = true
  Symmetric = false
FEATURE [Part::Extrusion] Extrude001
  Base = -> Ruled_Surface002
  Dir = (1,0,0)
  DirMode = 0
  FaceMakerClass = Part::FaceMakerBullseye
  LengthFwd = 50
  LengthRev = 0
  Solid = true
  Symmetric = false
FEATURE [Part::Extrusion] Extrude002
  Base = -> Ruled_Surface003
  Dir = (1,0,0)
  DirMode = 0
  FaceMakerClass = Part::FaceMakerBullseye
  LengthFwd = 50
  LengthRev = 0
  Solid = true
  Symmetric = false
FEATURE [Part::Extrusion] Extrude003
  Base = -> Ruled_Surface005
  Dir = (1,0,0)
  DirMode = 0
  FaceMakerClass = Part::FaceMakerBullseye
  LengthFwd = 50
  LengthRev = 0
  Solid = true
  Symmetric = false
FEATURE [Part::Extrusion] Extrude004
  Base = -> Ruled_Surface006
  Dir = (1,0,0)
  DirMode = 0
  FaceMakerClass = Part::FaceMakerBullseye
  LengthFwd = 50
  LengthRev = 0
  Solid = true
  Symmetric = false
FEATURE [Part::Extrusion] Extrude005
  Base = -> Ruled_Surface007
  Dir = (1,0,0)
  DirMode = 0
  FaceMakerClass = Part::FaceMakerBullseye
  LengthFwd = 50
  LengthRev = 0
  Solid = true
  Symmetric = false
FEATURE [Part::Extrusion] Extrude006
  Base = -> Ruled_Surface008
  Dir = (1,0,0)
  DirMode = 0
  FaceMakerClass = Part::FaceMakerBullseye
  LengthFwd = 50
  LengthRev = 0
  Solid = true
  Symmetric = false
FEATURE [Part::Extrusion] Extrude007
  Base = -> Ruled_Surface009
  Dir = (1,0,0)
  DirMode = 0
  FaceMakerClass = Part::FaceMakerBullseye
  LengthFwd = 50
  LengthRev = 0
  Solid = true
  Symmetric = false
FEATURE [Part::Extrusion] Extrude008
  Base = -> Ruled_Surface010
  Dir = (1,0,0)
  DirMode = 0
  FaceMakerClass = Part::FaceMakerBullseye
  LengthFwd = 50
  LengthRev = 0
  Solid = true
  Symmetric = false
FEATURE [Part::Extrusion] Extrude009
  Base = -> Ruled_Surface011
  Dir = (1,0,0)
  DirMode = 0
  FaceMakerClass = Part::FaceMakerBullseye
  LengthFwd = 50
  LengthRev = 0
  Solid = true
  Symmetric = false
FEATURE [Part::Extrusion] Extrude010
  Base = -> Ruled_Surface012
  Dir = (1,0,0)
  DirMode = 0
  FaceMakerClass = Part::FaceMakerBullseye
  LengthFwd = 50
  LengthRev = 0
  Solid = true
  Symmetric = false
FEATURE [Part::Extrusion] Extrude011
  Base = -> Ruled_Surface013
  Dir = (1,0,0)
  DirMode = 0
  FaceMakerClass = Part::FaceMakerBullseye
  LengthFwd = 50
  LengthRev = 0
  Solid = true
  Symmetric = false
FEATURE [Part::Extrusion] Extrude012
  Base = -> Ruled_Surface014
  Dir = (1,0,0)
  DirMode = 0
  FaceMakerClass = Part::FaceMakerBullseye
  LengthFwd = 50
  LengthRev = 0
  Solid = true
  Symmetric = false
FEATURE [Part::Extrusion] Extrude013
  Base = -> Ruled_Surface015
  Dir = (1,0,0)
  DirMode = 0
  FaceMakerClass = Part::FaceMakerBullseye
  LengthFwd = 50
  LengthRev = 0
  Solid = true
  Symmetric = false
FEATURE [Part::Extrusion] Extrude014
  Base = -> Ruled_Surface016
  Dir = (1,0,0)
  DirMode = 0
  FaceMakerClass = Part::FaceMakerBullseye
  LengthFwd = 50
  LengthRev = 0
  Solid = true
  Symmetric = false
FEATURE [App::DocumentObjectGroup] Group  label="Grupo"
FEATURE [Sketcher::SketchObject] Sketch007
  FullyConstrained = true
  Placement = pos=(0,0,0) rot=(1,0,0;1.5708rad)
  sketch-geometry (39):
    g0: LineSegment StartX=-55 StartY=55 StartZ=0 EndX=55 EndY=55 EndZ=0
    g1: LineSegment StartX=-55 StartY=55 StartZ=0 EndX=-55 EndY=-55 EndZ=0
    g2: LineSegment StartX=55 StartY=55 StartZ=0 EndX=55 EndY=-55 EndZ=0
    g3: LineSegment StartX=-55 StartY=-55 StartZ=0 EndX=55 EndY=-55 EndZ=0
    g4: GeomPoint X=72 Y=-55 Z=0
    g5: GeomPoint X=-72 Y=-55 Z=0
    g6: Circle CenterX=72 CenterY=-55 CenterZ=0 NormalX=0 NormalY=0 NormalZ=1 AngleXU=0 Radius=10
    g7: Circle CenterX=-72 CenterY=-55 CenterZ=0 NormalX=0 NormalY=0 NormalZ=1 AngleXU=0 Radius=10
    g8: Circle CenterX=0 CenterY=0 CenterZ=0 NormalX=0 NormalY=0 NormalZ=1 AngleXU=0 Radius=22
    g9: Circle CenterX=0 CenterY=0 CenterZ=0 NormalX=0 NormalY=0 NormalZ=1 AngleXU=0 Radius=29
    g10: Circle CenterX=72 CenterY=-55 CenterZ=0 NormalX=0 NormalY=0 NormalZ=1 AngleXU=0 Radius=13
    g11: Circle CenterX=-72 CenterY=-55 CenterZ=0 NormalX=0 NormalY=0 NormalZ=1 AngleXU=0 Radius=13
    g12: LineSegment StartX=-72 StartY=-55 StartZ=0 EndX=-81.1924 EndY=-45.8076 EndZ=0
    g13: LineSegment StartX=-72 StartY=-55 StartZ=0 EndX=-62.8076 EndY=-64.1924 EndZ=0
    g14: LineSegment StartX=72 StartY=-55 StartZ=0 EndX=81.1924 EndY=-45.8076 EndZ=0
    g15: LineSegment StartX=72 StartY=-55 StartZ=0 EndX=62.8076 EndY=-64.1924 EndZ=0
    g16: GeomPoint X=0 Y=-29 Z=0
    g17: GeomPoint X=29 Y=0 Z=0
    g18: GeomPoint X=-29 Y=0 Z=0
    g19: LineSegment StartX=-81.1924 StartY=-45.8076 StartZ=0 EndX=-29 EndY=0 EndZ=0
    g20: LineSegment StartX=29 StartY=0 StartZ=0 EndX=81.1924 EndY=-45.8076 EndZ=0
    g21: LineSegment StartX=-62.8076 StartY=-64.1924 StartZ=0 EndX=0 EndY=-29 EndZ=0
    g22: LineSegment StartX=62.8076 StartY=-64.1924 StartZ=0 EndX=0 EndY=-29 EndZ=0
    g23: LineSegment StartX=-55 StartY=-37.5 StartZ=0 EndX=-55 EndY=37.5 EndZ=0
    g24: LineSegment StartX=-55 StartY=37.5 StartZ=0 EndX=-37.5 EndY=55 EndZ=0
    g25: LineSegment StartX=-37.5 StartY=55 StartZ=0 EndX=37.5 EndY=55 EndZ=0
    g26: LineSegment StartX=37.5 StartY=55 StartZ=0 EndX=55 EndY=37.5 EndZ=0
    g27: LineSegment StartX=55 StartY=37.5 StartZ=0 EndX=55 EndY=-37.5 EndZ=0
    g28: LineSegment StartX=37.5 StartY=-55 StartZ=0 EndX=55 EndY=-37.5 EndZ=0
    g29: LineSegment StartX=37.5 StartY=-55 StartZ=0 EndX=-37.5 EndY=-55 EndZ=0
    g30: LineSegment StartX=-55 StartY=-37.5 StartZ=0 EndX=-37.5 EndY=-55 EndZ=0
    g31: LineSegment StartX=-27.6807 StartY=-1.50316 StartZ=0 EndX=-79.8731 EndY=-47.3108 EndZ=0
    g32: LineSegment StartX=79.8731 StartY=-47.3108 StartZ=0 EndX=27.6807 EndY=-1.50316 EndZ=0
    g33: LineSegment StartX=27.6807 StartY=-1.50316 StartZ=0 EndX=29 EndY=0 EndZ=0
    g34: LineSegment StartX=-29 StartY=0 StartZ=0 EndX=-27.6807 EndY=-1.50316 EndZ=0
    g35: LineSegment StartX=-63.7852 StartY=-62.4476 StartZ=0 EndX=-0.977632 EndY=-27.2552 EndZ=0
    g36: LineSegment StartX=0.977632 StartY=-27.2552 StartZ=0 EndX=63.7852 EndY=-62.4476 EndZ=0
    g37: LineSegment StartX=-0.977632 StartY=-27.2552 StartZ=0 EndX=0 EndY=-29 EndZ=0
    g38: LineSegment StartX=0 StartY=-29 StartZ=0 EndX=0.977632 EndY=-27.2552 EndZ=0
  constraints (102):
    c: Horizontal(g0)
    c: DistanceY(g-1,g0) = 55
    c: DistanceX(g0,g-1) = 55
    c: DistanceX(g0,g0) = 110
    c: Coincident(g1,g0)
    c: Vertical(g1)
    c: DistanceY(g1,g0) = 110
    c: Coincident(g2,g0)
    c: Vertical(g2)
    c: Coincident(g3,g1)
    c: Coincident(g3,g2)
    c: Horizontal(g3)
    c: DistanceY(g4,g0) = 110
    c: DistanceX(g-1,g4) = 72
    c: Coincident(g6,g4)
    c: Diameter(g6) = 20
    c: Horizontal(g5,g6)
    c: DistanceX(g5,g6) = 144
    c: Coincident(g7,g5)
    c: Diameter(g7) = 20
    c: Coincident(g8,g-1)
    c: Diameter(g8) = 44
    c: Coincident(g9,g8)
    c: Diameter(g9) = 58
    c: Coincident(g10,g6)
    c: Diameter(g10) = 26
    c: Coincident(g11,g7)
    c: Diameter(g11) = 26
    c: Coincident(g12,g7)
    c: PointOnObject(g12,g11)
    c: Angle(g3,g12) = 2.35619
    c: Coincident(g13,g7)
    c: PointOnObject(g13,g11)
    c: Angle(g12,g13) = 3.14159
    c: Coincident(g14,g6)
    c: PointOnObject(g14,g10)
    c: Coincident(g15,g6)
    c: PointOnObject(g15,g10)
    c: Angle(g14,g3) = 2.35619
    c: Angle(g15,g14) = 3.14159
    c: PointOnObject(g16,g9)
    c: Vertical(g16,g8)
    c: PointOnObject(g17,g9)
    c: PointOnObject(g18,g9)
    c: Horizontal(g17,g8)
    c: Horizontal(g18,g8)
    c: Coincident(g22,g15)
    c: Coincident(g22,g16)
    c: Coincident(g21,g22)
    c: Coincident(g21,g13)
    c: Coincident(g19,g12)
    c: Coincident(g19,g18)
    c: Coincident(g20,g17)
    c: Coincident(g20,g14)
    c: Horizontal(g25)
    c: DistanceX(g25,g8) = 37.5
    c: DistanceX(g25,g25) = 75
    c: Horizontal(g25,g0)
    c: DistanceY(g8,g27) = 37.5
    c: Vertical(g27,g27)
    c: DistanceY(g27,g27) = 75
    c: Vertical(g27,g0)
    c: Horizontal(g27,g23)
    c: Horizontal(g27,g23)
    c: Vertical(g23,g23)
    c: Vertical(g23,g1)
    c: Coincident(g24,g25)
    c: Coincident(g24,g23)
    c: Coincident(g26,g25)
    c: Coincident(g26,g27)
    c: Vertical(g29,g24)
    c: Vertical(g29,g25)
    c: Horizontal(g29,g29)
    c: Horizontal(g29,g1)
    c: Coincident(g30,g23)
    c: Coincident(g29,g30)
    c: Coincident(g28,g29)
    c: Coincident(g28,g27)
    c: Coincident(g20,g33)
    c: Angle(g33,g20) = 1.5708
    c: Distance(g20,g33) = 2
    c: Angle(g20,g32) = 0
    c: Coincident(g33,g32)
    c: Distance(g14,g32) = 2
    c: Coincident(g19,g34)
    c: Angle(g19,g34) = 1.5708
    c: Distance(g19,g34) = 2
    c: Angle(g19,g31) = 0
    c: Coincident(g34,g31)
    c: Distance(g12,g31) = 2
    c: Coincident(g37,g21)
    c: Coincident(g21,g38)
    c: Angle(g37,g21) = 1.5708
    c: Angle(g22,g38) = 1.5708
    c: Angle(g21,g35) = 0
    c: Angle(g36,g22) = 0
    c: Distance(g21,g37) = 2
    c: Horizontal(g38,g37)
    c: Coincident(g36,g38)
    c: Coincident(g35,g37)
    c: Distance(g15,g36) = 2
    c: Distance(g13,g35) = 2
FEATURE [Sketcher::SketchObject] Sketch008
  ExternalGeometry = -> [Sketch007]
  FullyConstrained = false
  MapMode = 4
  sketch-geometry (17):
    g0: LineSegment StartX=55 StartY=-1.8e-15 StartZ=0 EndX=55 EndY=-110 EndZ=0
    g1: LineSegment StartX=55 StartY=0 StartZ=0 EndX=55 EndY=-110 EndZ=0
    g2: LineSegment StartX=55 StartY=-110 StartZ=0 EndX=55 EndY=-110 EndZ=0
    g3: LineSegment StartX=-29 StartY=0 StartZ=0 EndX=29 EndY=0 EndZ=0
    g4: LineSegment StartX=-29 StartY=7 StartZ=0 EndX=-29 EndY=0 EndZ=0
    g5: LineSegment StartX=29 StartY=7 StartZ=0 EndX=29 EndY=0 EndZ=0
    g6: LineSegment StartX=29 StartY=7 StartZ=0 EndX=-29 EndY=7 EndZ=0
    g7: LineSegment StartX=-29 StartY=-117 StartZ=0 EndX=29 EndY=-117 EndZ=0
    g8: LineSegment StartX=29 StartY=-110 StartZ=0 EndX=29 EndY=-117 EndZ=0
    g9: LineSegment StartX=-29 StartY=-110 StartZ=0 EndX=-29 EndY=-117 EndZ=0
    g10: LineSegment StartX=-29.1576 StartY=-110 StartZ=0 EndX=29 EndY=-110 EndZ=0
    g11: LineSegment StartX=-29 StartY=0 StartZ=0 EndX=29 EndY=0 EndZ=0
    g12: LineSegment StartX=-72 StartY=-155 StartZ=0 EndX=-72 EndY=-185 EndZ=0
    g13: LineSegment StartX=72 StartY=-155 StartZ=0 EndX=72 EndY=-185 EndZ=0
    g14: LineSegment StartX=72 StartY=0 StartZ=0 EndX=72 EndY=-20 EndZ=0
    g15: LineSegment StartX=-72 StartY=0 StartZ=0 EndX=-72 EndY=-20 EndZ=0
    g16: LineSegment StartX=0 StartY=-6.4e-15 StartZ=0 EndX=0 EndY=-110 EndZ=0
  constraints (57):
    c: Coincident(g0,g-5)
    c: DistanceY(g0,g0) = 110
    c: Vertical(g0,g0)
    c: Coincident(g1,g-5)
    c: Horizontal(g0,g1)
    c: Vertical(g1,g1)
    c: Coincident(g2,g0)
    c: Coincident(g2,g1)
    c: Horizontal(g3)
    c: DistanceX(g3,g3) = 58
    c: DistanceX(g3,g-1) = 29
    c: Horizontal(g-1,g3)
    c: Vertical(g4)
    c: Vertical(g5)
    c: DistanceY(g4,g4) = 7
    c: Coincident(g3,g4)
    c: Coincident(g3,g5)
    c: Horizontal(g4,g5)
    c: Coincident(g6,g4)
    c: Coincident(g5,g6)
    c: Horizontal(g7)
    c: Vertical(g3,g9)
    c: Vertical(g3,g9)
    c: Vertical(g5,g8)
    c: Vertical(g3,g8)
    c: Horizontal(g9,g1)
    c: Horizontal(g0,g8)
    c: Vertical(g3,g7)
    c: Vertical(g5,g7)
    c: DistanceY(g9,g9) = 7
    c: Horizontal(g9,g7)
    c: Horizontal(g7,g8)
    c: Horizontal(g10)
    c: Vertical(g8,g10)
    c: Horizontal(g10,g9)
    c: Horizontal(g11)
    c: Vertical(g3,g11)
    c: Vertical(g3,g11)
    c: Horizontal(g3,g11)
    c: Vertical(g12)
    c: Vertical(g13)
    c: DistanceY(g12,g12) = 30
    c: Horizontal(g12,g13)
    c: Horizontal(g12,g13)
    c: Vertical(g14)
    c: Vertical(g15)
    c: DistanceY(g14,g14) = 20
    c: Horizontal(g14,g15)
    c: PointOnObject(g16,g-2)
    c: PointOnObject(g16,g-2)
    c: Horizontal(g-4,g16)
    c: Horizontal(g16,g8)
    c: DistanceX(g16,g14) = 72
    c: DistanceX(g15,g14) = 144
    c: Vertical(g15,g12)
    c: Vertical(g14,g13)
    c: DistanceY(g12,g15) = 135
FEATURE [Sketcher::SketchObject] Sketch009
  ExternalGeometry = -> [Sketch007]
  FullyConstrained = true
  Placement = pos=(0,0,0) rot=(1,0,0;1.5708rad)
  sketch-geometry (9):
    g0: LineSegment StartX=-62.8076 StartY=-64.1924 StartZ=0 EndX=0.977632 EndY=-27.2552 EndZ=0
    g1: LineSegment StartX=-55 StartY=37.5 StartZ=0 EndX=-55 EndY=-37.5 EndZ=0
    g2: LineSegment StartX=-55 StartY=37.5 StartZ=0 EndX=-37.5 EndY=55 EndZ=0
    g3: LineSegment StartX=-37.5 StartY=55 StartZ=0 EndX=37.5 EndY=55 EndZ=0
    g4: LineSegment StartX=37.5 StartY=55 StartZ=0 EndX=55 EndY=37.5 EndZ=0
    g5: LineSegment StartX=55 StartY=37.5 StartZ=0 EndX=55 EndY=-37.5 EndZ=0
    g6: LineSegment StartX=37.5 StartY=-55 StartZ=0 EndX=-37.5 EndY=-55 EndZ=0
    g7: LineSegment StartX=37.5 StartY=-55 StartZ=0 EndX=55 EndY=-37.5 EndZ=0
    g8: LineSegment StartX=-55 StartY=-37.5 StartZ=0 EndX=-37.5 EndY=-55 EndZ=0
  constraints (36):
    c: Horizontal(g-5,g0)
    c: Vertical(g-5,g0)
    c: Vertical(g-4,g0)
    c: Horizontal(g-4,g0)
    c: Vertical(g1)
    c: Horizontal(g3)
    c: Horizontal(g6)
    c: Vertical(g5,g5)
    c: Horizontal(g-16,g5)
    c: Horizontal(g-17,g5)
    c: Horizontal(g-17,g1)
    c: Horizontal(g-13,g1)
    c: Horizontal(g2,g-13)
    c: Horizontal(g-13,g4)
    c: Horizontal(g-17,g7)
    c: Horizontal(g-18,g8)
    c: Horizontal(g-19,g7)
    c: Horizontal(g-20,g8)
    c: Vertical(g-14,g3)
    c: Vertical(g-15,g3)
    c: Vertical(g4,g-15)
    c: Vertical(g4,g-16)
    c: Vertical(g5,g4)
    c: Vertical(g2,g-13)
    c: Vertical(g1,g2)
    c: Vertical(g2,g-14)
    c: Vertical(g-20,g6)
    c: Vertical(g-19,g6)
    c: Vertical(g-19,g7)
    c: Vertical(g8,g-20)
    c: Vertical(g8,g1)
    c: Vertical(g5,g7)
    c: Horizontal(g3,g-15)
    c: Horizontal(g2,g3)
    c: Horizontal(g4,g3)
    c: Horizontal(g7,g6)
FEATURE [Part::RuledSurface] Ruled_Surface017
  Curve1 = -> Sketch007 [Edge11]
  Curve2 = -> Sketch007 [Edge8]
  Orientation = 0
FEATURE [Part::RuledSurface] Ruled_Surface018
  Curve1 = -> Sketch007 [Edge24]
  Curve2 = -> Sketch007 [Edge14]
  Orientation = 0
FEATURE [Part::RuledSurface] Ruled_Surface019
  Curve1 = -> Sketch007 [Edge16]
  Curve2 = -> Sketch007 [Edge22]
  Orientation = 0
FEATURE [Part::RuledSurface] Ruled_Surface020
  Curve1 = -> Sketch007 [Edge19]
  Curve2 = -> Sketch007 [Edge17]
  Orientation = 0
FEATURE [Part::Extrusion] Extrude015
  Base = -> Ruled_Surface017
  Dir = (0,-110,0)
  DirLink = -> Sketch008 [Edge1]
  DirMode = 1
  FaceMakerClass = Part::FaceMakerBullseye
  LengthFwd = 20
  LengthRev = 0
  Solid = true
  Symmetric = false
FEATURE [Part::Extrusion] Extrude016
  Base = -> Ruled_Surface018
  Dir = (0,-110,0)
  DirLink = -> Sketch008 [Edge1]
  DirMode = 1
  FaceMakerClass = Part::FaceMakerBullseye
  LengthFwd = 20
  LengthRev = 0
  Solid = true
  Symmetric = false
FEATURE [Part::Extrusion] Extrude017
  Base = -> Ruled_Surface019
  Dir = (0,-110,0)
  DirLink = -> Sketch008 [Edge1]
  DirMode = 1
  FaceMakerClass = Part::FaceMakerBullseye
  LengthFwd = 20
  LengthRev = 0
  Solid = true
  Symmetric = false
FEATURE [Part::Extrusion] Extrude018
  Base = -> Ruled_Surface020
  Dir = (0,-110,0)
  DirLink = -> Sketch008 [Edge1]
  DirMode = 1
  FaceMakerClass = Part::FaceMakerBullseye
  LengthFwd = 20
  LengthRev = 0
  Solid = true
  Symmetric = false
FEATURE [Part::RuledSurface] Ruled_Surface004
  Curve1 = -> Sketch007 [Edge5]
  Curve2 = -> Sketch007 [Edge25]
  Orientation = 0
FEATURE [Part::Extrusion] Extrude019
  Base = -> Ruled_Surface004
  Dir = (0,-110,0)
  DirLink = -> Sketch008 [Edge1]
  DirMode = 1
  FaceMakerClass = Part::FaceMakerBullseye
  LengthFwd = 20
  LengthRev = 0
  Solid = true
  Symmetric = false
FEATURE [Part::RuledSurface] Ruled_Surface021
  Curve1 = -> Sketch007 [Edge26]
  Curve2 = -> Sketch007 [Edge6]
  Orientation = 0
FEATURE [Part::Extrusion] Extrude020
  Base = -> Ruled_Surface021
  Dir = (0,-110,0)
  DirLink = -> Sketch008 [Edge1]
  DirMode = 1
  FaceMakerClass = Part::FaceMakerBullseye
  LengthFwd = 20
  LengthRev = 0
  Solid = true
  Symmetric = false
FEATURE [Part::Extrusion] Extrude021
  Base = -> Ruled_Surface021
  Dir = (0,-110,0)
  DirLink = -> Sketch008 [Edge1]
  DirMode = 1
  FaceMakerClass = Part::FaceMakerBullseye
  LengthFwd = 30
  LengthRev = 0
  Placement = pos=(0,-155,0) rot=(0,0,1;0rad)
  Solid = true
  Symmetric = false
FEATURE [Part::Extrusion] Extrude022
  Base = -> Ruled_Surface004
  Dir = (0,-110,0)
  DirLink = -> Sketch008 [Edge1]
  DirMode = 1
  FaceMakerClass = Part::FaceMakerBullseye
  LengthFwd = 30
  LengthRev = 0
  Placement = pos=(0,-155,0) rot=(0,0,1;0rad)
  Solid = true
  Symmetric = false
FEATURE [Part::RuledSurface] Ruled_Surface022
  Curve1 = -> Sketch009 [Edge3]
  Curve2 = -> Sketch009 [Edge7]
  Orientation = 0
FEATURE [Part::RuledSurface] Ruled_Surface023
  Curve1 = -> Sketch009 [Edge4]
  Curve2 = -> Sketch009 [Edge6]
  Orientation = 0
FEATURE [Part::RuledSurface] Ruled_Surface024
  Curve1 = -> Sketch009 [Edge2]
  Curve2 = -> Sketch009 [Edge8]
  Orientation = 0
FEATURE [Part::FeaturePython] Connect  # WARN: FeaturePython — macro-defined, semantics opaque (R4)
  Objects = -> [Ruled_Surface022,Ruled_Surface024,Ruled_Surface023]
  Tolerance = 0
FEATURE [Part::RuledSurface] Ruled_Surface025
  Curve1 = -> Sketch007 [Edge7]
  Curve2 = -> Sketch007 [Edge10]
  Orientation = 0
FEATURE [Part::Extrusion] Extrude023
  Base = -> Ruled_Surface025
  Dir = (0,-110,0)
  DirLink = -> Sketch008 [Edge1]
  DirMode = 1
  FaceMakerClass = Part::FaceMakerBullseye
  LengthFwd = 0
  LengthRev = 7
  Solid = true
  Symmetric = false
FEATURE [Part::Extrusion] Extrude024
  Base = -> Ruled_Surface025
  Dir = (0,-110,0)
  DirLink = -> Sketch008 [Edge1]
  DirMode = 1
  FaceMakerClass = Part::FaceMakerBullseye
  LengthFwd = 0
  LengthRev = 7
  Placement = pos=(0,-117,0) rot=(0,0,1;0rad)
  Solid = true
  Symmetric = false
FEATURE [Part::Extrusion] Extrude025
  Base = -> Connect
  Dir = (0,-110,0)
  DirLink = -> Sketch008 [Edge17]
  DirMode = 1
  FaceMakerClass = Part::FaceMakerBullseye
  LengthFwd = 0
  LengthRev = 0
  Solid = true
  Symmetric = false
FEATURE [Part::RuledSurface] Ruled_Surface026
  Curve1 = -> Extrude015 [Edge4]
  Curve2 = -> Extrude016 [Edge4]
  Orientation = 0
FEATURE [Part::Extrusion] Extrude026
  Base = -> Ruled_Surface026
  Dir = (0,1,0)
  DirMode = 0
  FaceMakerClass = Part::FaceMakerBullseye
  LengthFwd = 2
  LengthRev = 0
  Solid = true
  Symmetric = false
FEATURE [Sketcher::SketchObject] Sketch010
  ExternalGeometry = -> [Sketch007]
  FullyConstrained = false
  Placement = pos=(0,0,0) rot=(1,0,0;1.5708rad)
  sketch-geometry (4):
    g0: GeomPoint X=-72 Y=-55 Z=0
    g1: Circle CenterX=-72 CenterY=-55 CenterZ=0 NormalX=0 NormalY=0 NormalZ=1 AngleXU=0 Radius=10
    g2: GeomPoint X=72 Y=-55 Z=0
    g3: Circle CenterX=72 CenterY=-55 CenterZ=0 NormalX=0 NormalY=0 NormalZ=1 AngleXU=0 Radius=10
  constraints (4):
    c: Coincident(g0,g-3)
    c: Coincident(g1,g0)
    c: Coincident(g2,g-4)
    c: Coincident(g3,g2)
FEATURE [Part::Face] Face
  FaceMakerClass = Part::FaceMakerBullseye
  Sources = -> [Sketch010]
FEATURE [Part::MultiFuse] Fusion001
  Shapes = -> [Extrude026,Extrude015,Extrude016,Extrude019]
FEATURE [Part::Extrusion] Extrude027
  Base = -> Face
  Dir = (0,-1,0)
  DirLink = -> Sketch008 [Edge15]
  DirMode = 0
  FaceMakerClass = Part::FaceMakerBullseye
  LengthFwd = 30
  LengthRev = 0
  Solid = false
  Symmetric = false
FEATURE [Part::Cut] Cut
  Base = -> Fusion001
  Tool = -> Extrude027
FEATURE [Part::RuledSurface] Ruled_Surface027
  Curve1 = -> Extrude018 [Edge4]
  Curve2 = -> Extrude017 [Edge10]
  Orientation = 0
FEATURE [Part::Extrusion] Extrude028
  Base = -> Ruled_Surface027
  Dir = (0,1,0)
  DirMode = 0
  FaceMakerClass = Part::FaceMakerBullseye
  LengthFwd = 2
  LengthRev = 0
  Solid = true
  Symmetric = false
FEATURE [Part::MultiFuse] Fusion003
  Shapes = -> [Extrude028,Extrude020,Extrude017,Extrude018]
FEATURE [Part::Cut] Cut001
  Base = -> Fusion003
  Tool = -> Extrude027
FEATURE [Part::Extrusion] Extrude029
  Base = -> Ruled_Surface017
  Dir = (0,-1,0)
  DirMode = 0
  FaceMakerClass = Part::FaceMakerBullseye
  LengthFwd = 185
  LengthRev = 0
  Solid = false
  Symmetric = false
FEATURE [Part::Extrusion] Extrude030
  Base = -> Ruled_Surface018
  Dir = (0,-1,0)
  DirMode = 0
  FaceMakerClass = Part::FaceMakerBullseye
  LengthFwd = 185
  LengthRev = 0
  Solid = false
  Symmetric = false
FEATURE [Part::Extrusion] Extrude031
  Base = -> Ruled_Surface019
  Dir = (0,-1,0)
  DirMode = 0
  FaceMakerClass = Part::FaceMakerBullseye
  LengthFwd = 185
  LengthRev = 0
  Solid = true
  Symmetric = false
FEATURE [Part::Extrusion] Extrude032
  Base = -> Ruled_Surface020
  Dir = (0,-1,0)
  DirMode = 0
  FaceMakerClass = Part::FaceMakerBullseye
  LengthFwd = 185
  LengthRev = 0
  Solid = true
  Symmetric = false
FEATURE [Sketcher::SketchObject] Sketch011
  ExternalGeometry = -> [Sketch008]
  FullyConstrained = false
  sketch-geometry (14):
    g0: GeomPoint X=55 Y=-55 Z=0
    g1: LineSegment StartX=55 StartY=-54.9128 StartZ=0 EndX=55 EndY=-155 EndZ=0
    g2: GeomPoint X=-55 Y=-54.9128 Z=0
    g3: LineSegment StartX=-55 StartY=-54.9128 StartZ=0 EndX=-55 EndY=-155 EndZ=0
    g4: LineSegment StartX=55 StartY=-155 StartZ=0 EndX=85 EndY=-155 EndZ=0
    g5: LineSegment StartX=-85 StartY=-155 StartZ=0 EndX=-55 EndY=-155 EndZ=0
    g6: LineSegment StartX=-85 StartY=-175 StartZ=0 EndX=-42 EndY=-175 EndZ=0
    g7: LineSegment StartX=85 StartY=-175 StartZ=0 EndX=42 EndY=-175 EndZ=0
    g8: LineSegment StartX=-29.1576 StartY=-110 StartZ=0 EndX=-42 EndY=-175 EndZ=0
    g9: LineSegment StartX=29 StartY=-110 StartZ=0 EndX=42 EndY=-175 EndZ=0
    g10: LineSegment StartX=-85 StartY=-155 StartZ=0 EndX=-85 EndY=-175 EndZ=0
    g11: LineSegment StartX=85 StartY=-155 StartZ=0 EndX=85 EndY=-175 EndZ=0
    g12: LineSegment StartX=-55 StartY=-54.9128 StartZ=0 EndX=55 EndY=-54.9128 EndZ=0
    g13: LineSegment StartX=-29.1576 StartY=-110 StartZ=0 EndX=29 EndY=-110 EndZ=0
  constraints (37):
    c: DistanceY(g0,g-1) = 55
    c: DistanceX(g-1,g0) = 55
    c: Vertical(g1)
    c: Vertical(g0,g1)
    c: Horizontal(g-3,g1)
    c: Horizontal(g1,g2)
    c: DistanceX(g2,g1) = 110
    c: Vertical(g3)
    c: Coincident(g2,g3)
    c: Horizontal(g1,g3)
    c: Horizontal(g4)
    c: Coincident(g4,g1)
    c: Coincident(g3,g5)
    c: Horizontal(g3,g5)
    c: DistanceX(g5,g3) = 30
    c: DistanceX(g1,g4) = 30
    c: Horizontal(g6)
    c: Horizontal(g7)
    c: DistanceY(g6,g5) = 20
    c: Horizontal(g6,g7)
    c: Vertical(g5,g6)
    c: Vertical(g4,g7)
    c: DistanceX(g-4,g6) = 30
    c: Coincident(g6,g8)
    c: Coincident(g8,g-5)
    c: DistanceX(g7,g-3) = 30
    c: Coincident(g-5,g9)
    c: Coincident(g9,g7)
    c: Vertical(g10)
    c: Coincident(g10,g5)
    c: Horizontal(g6,g10)
    c: Coincident(g11,g4)
    c: Coincident(g11,g7)
    c: Coincident(g12,g3)
    c: Coincident(g12,g1)
    c: Coincident(g13,g8)
    c: Coincident(g13,g9)
FEATURE [Part::Face] Face001
  FaceMakerClass = Part::FaceMakerBullseye
  Sources = -> [Sketch011]
FEATURE [Part::Extrusion] Extrude033
  Base = -> Face001
  Dir = (0,0,-1)
  DirMode = 0
  FaceMakerClass = Part::FaceMakerBullseye
  LengthFwd = 70
  LengthRev = 0
  Solid = true
  Symmetric = false
FEATURE [Part::MultiCommon] Common001
  Shapes = -> [Extrude033,Extrude029]
FEATURE [Sketcher::SketchObject] Sketch012
  ExternalGeometry = -> [Sketch011,Sketch008]
  FullyConstrained = false
  sketch-geometry (12):
    g0: LineSegment StartX=5 StartY=-110 StartZ=0 EndX=18 EndY=-175 EndZ=0
    g1: LineSegment StartX=-5 StartY=-110 StartZ=0 EndX=-17.8424 EndY=-175 EndZ=0
    g2: LineSegment StartX=-85 StartY=-155 StartZ=0 EndX=-85 EndY=-175 EndZ=0
    g3: LineSegment StartX=-17.8424 StartY=-175 StartZ=0 EndX=-85 EndY=-175 EndZ=0
    g4: LineSegment StartX=85 StartY=-155 StartZ=0 EndX=85 EndY=-175 EndZ=0
    g5: LineSegment StartX=85 StartY=-175 StartZ=0 EndX=18 EndY=-175 EndZ=0
    g6: LineSegment StartX=5 StartY=-110 StartZ=0 EndX=-5 EndY=-110 EndZ=0
    g7: LineSegment StartX=-47.5 StartY=-54.9128 StartZ=0 EndX=47.5 EndY=-54.9128 EndZ=0
    g8: LineSegment StartX=-47.5 StartY=-54.9128 StartZ=0 EndX=-47.5 EndY=-155 EndZ=0
    g9: LineSegment StartX=47.5 StartY=-54.9128 StartZ=0 EndX=47.5 EndY=-155 EndZ=0
    g10: LineSegment StartX=-85 StartY=-155 StartZ=0 EndX=-47.5 EndY=-155 EndZ=0
    g11: LineSegment StartX=47.5 StartY=-155 StartZ=0 EndX=85 EndY=-155 EndZ=0
  constraints (31):
    c: DistanceX(g-1,g0) = 5
    c: DistanceX(g1,g-1) = 5
    c: Horizontal(g-11,g1)
    c: Horizontal(g-11,g0)
    c: Angle(g1,g-12) = 0
    c: Angle(g-13,g0) = 0
    c: Horizontal(g-12,g1)
    c: Horizontal(g-13,g0)
    c: Coincident(g2,g-6)
    c: Coincident(g2,g-6)
    c: Coincident(g3,g1)
    c: Coincident(g3,g2)
    c: Coincident(g4,g-7)
    c: Coincident(g5,g4)
    c: Coincident(g5,g0)
    c: Coincident(g6,g0)
    c: Coincident(g6,g1)
    c: Horizontal(g7)
    c: Horizontal(g-3,g7)
    c: DistanceX(g-3,g7) = 7.5
    c: DistanceX(g7,g-4) = 7.5
    c: Coincident(g8,g7)
    c: Vertical(g8)
    c: Coincident(g9,g7)
    c: Vertical(g9)
    c: Horizontal(g2,g8)
    c: Horizontal(g4,g9)
    c: Coincident(g10,g2)
    c: Coincident(g10,g8)
    c: Coincident(g11,g9)
    c: Coincident(g11,g4)
FEATURE [Part::MultiCommon] Common
  Shapes = -> [Extrude033,Extrude032]
FEATURE [Part::Face] Face002
  FaceMakerClass = Part::FaceMakerBullseye
  Sources = -> [Sketch012]
FEATURE [Part::Extrusion] Extrude034
  Base = -> Sketch012
  Dir = (0,0,-1)
  DirMode = 0
  FaceMakerClass = Part::FaceMakerBullseye
  LengthFwd = 80
  LengthRev = 0
  Solid = true
  Symmetric = false
FEATURE [Part::MultiCommon] Common002
  Shapes = -> [Extrude031,Extrude034]
FEATURE [Part::MultiCommon] Common003
  Shapes = -> [Extrude030,Extrude034]
FEATURE [Part::RuledSurface] Ruled_Surface028
  Curve1 = -> Common [Edge6]
  Curve2 = -> Common [Edge14]
  Orientation = 0
FEATURE [Part::Extrusion] Extrude035
  Base = -> Ruled_Surface028
  Dir = (0,0,-1)
  DirMode = 0
  FaceMakerClass = Part::FaceMakerBullseye
  LengthFwd = 25
  LengthRev = 0
  Solid = false
  Symmetric = false
FEATURE [Part::RuledSurface] Ruled_Surface029
  Curve1 = -> Common001 [Edge6]
  Curve2 = -> Common001 [Edge12]
  Orientation = 0
FEATURE [Part::Extrusion] Extrude036
  Base = -> Ruled_Surface029
  Dir = (0,0,-1)
  DirMode = 0
  FaceMakerClass = Part::FaceMakerBullseye
  LengthFwd = 25
  LengthRev = 0
  Solid = false
  Symmetric = false
FEATURE [Part::RuledSurface] Ruled_Surface030
  Curve1 = -> Extrude036 [Edge3]
  Curve2 = -> Extrude036 [Edge10]
  Orientation = 0
FEATURE [Part::RuledSurface] Ruled_Surface031
  Curve1 = -> Extrude035 [Edge3]
  Curve2 = -> Extrude035 [Edge10]
  Orientation = 0
FEATURE [Part::Extrusion] Extrude037
  Base = -> Ruled_Surface030
  Dir = (-1,0,0)
  DirMode = 0
  FaceMakerClass = Part::FaceMakerBullseye
  LengthFwd = 2
  LengthRev = 0
  Solid = true
  Symmetric = false
FEATURE [Part::Extrusion] Extrude038
  Base = -> Ruled_Surface031
  Dir = (1,0,0)
  DirMode = 0
  FaceMakerClass = Part::FaceMakerBullseye
  LengthFwd = 2
  LengthRev = 0
  Solid = true
  Symmetric = false
FEATURE [Part::RuledSurface] Ruled_Surface032
  Curve1 = -> Common002 [Edge12]
  Curve2 = -> Extrude038 [Edge9]
  Orientation = 0
FEATURE [Part::RuledSurface] Ruled_Surface033
  Curve1 = -> Extrude037 [Edge9]
  Curve2 = -> Common003 [Edge13]
  Orientation = 0
FEATURE [Sketcher::SketchObject] Sketch013
  ExternalGeometry = -> [Ruled_Surface033]
  FullyConstrained = true
  Placement = pos=(0,0,0) rot=(1,0,0;1.5708rad)
FEATURE [Part::Extrusion] Extrude039
  Base = -> Ruled_Surface033
  Dir = (-5.13,0,7.5)
  DirMode = 0
  FaceMakerClass = Part::FaceMakerBullseye
  LengthFwd = 2
  LengthRev = 0
  Solid = true
  Symmetric = false
FEATURE [Part::Extrusion] Extrude040
  Base = -> Ruled_Surface032
  Dir = (5.13,0,7.5)
  DirMode = 0
  FaceMakerClass = Part::FaceMakerBullseye
  LengthFwd = 2
  LengthRev = 0
  Solid = true
  Symmetric = false
FEATURE [Part::RuledSurface] Ruled_Surface034
  Curve1 = -> Extrude037 [Edge7]
  Curve2 = -> Common001 [Edge13]
  Orientation = 0
FEATURE [Part::RuledSurface] Ruled_Surface035
  Curve1 = -> Ruled_Surface034 [Edge2]
  Curve2 = -> Common003 [Edge3]
  Orientation = 0
FEATURE [Part::RuledSurface] Ruled_Surface036
  Curve1 = -> Ruled_Surface035 [Edge2]
  Curve2 = -> Extrude039 [Edge7]
  Orientation = 0
FEATURE [Part::RuledSurface] Ruled_Surface037
  Curve1 = -> Extrude038 [Edge7]
  Curve2 = -> Common [Edge5]
  Orientation = 0
FEATURE [Part::RuledSurface] Ruled_Surface038
  Curve1 = -> Common002 [Edge1]
  Curve2 = -> Ruled_Surface037 [Edge4]
  Orientation = 0
FEATURE [Part::RuledSurface] Ruled_Surface039
  Curve1 = -> Ruled_Surface038 [Edge2]
  Curve2 = -> Extrude040 [Edge7]
  Orientation = 0
FEATURE [Part::Extrusion] Extrude041
  Base = -> Ruled_Surface034
  Dir = (0,-1,0)
  DirMode = 0
  FaceMakerClass = Part::FaceMakerBullseye
  LengthFwd = 2
  LengthRev = 0
  Solid = true
  Symmetric = false
FEATURE [Part::Extrusion] Extrude042
  Base = -> Ruled_Surface036
  Dir = (0,-1,0)
  DirMode = 0
  FaceMakerClass = Part::FaceMakerBullseye
  LengthFwd = 2
  LengthRev = 0
  Solid = true
  Symmetric = false
FEATURE [Part::Extrusion] Extrude043
  Base = -> Ruled_Surface037
  Dir = (0,-1,0)
  DirMode = 0
  FaceMakerClass = Part::FaceMakerBullseye
  LengthFwd = 2
  LengthRev = 0
  Solid = true
  Symmetric = false
FEATURE [Part::Extrusion] Extrude044
  Base = -> Ruled_Surface039
  Dir = (0,-1,0)
  DirMode = 0
  FaceMakerClass = Part::FaceMakerBullseye
  LengthFwd = 2
  LengthRev = 0
  Solid = true
  Symmetric = false
FEATURE [Part::Extrusion] Extrude045
  Base = -> Face
  Dir = (0,-1,0)
  DirMode = 0
  FaceMakerClass = Part::FaceMakerBullseye
  LengthFwd = 200
  LengthRev = 0
  Solid = true
  Symmetric = false
FEATURE [Part::MultiFuse] Fusion004
  Shapes = -> [Extrude043,Extrude044,Extrude041,Extrude042]
FEATURE [Part::MultiFuse] Fusion005
  Shapes = -> [Extrude040,Extrude038,Fusion004,Common002,Common,Extrude021,Common003,Common001,Extrude039,Extrude037,Extrude022]
FEATURE [Part::MultiFuse] Fusion006
  Shapes = -> [Cut,Cut001]
FEATURE [Part::MultiFuse] Fusion007
  Shapes = -> [Extrude023,Extrude024,Extrude025]
FEATURE [Sketcher::SketchObject] Sketch014
  ExternalGeometry = -> [Sketch007]
  FullyConstrained = false
  Placement = pos=(0,-110,0) rot=(1,0,0;1.5708rad)
  sketch-geometry (1):
    g0: Circle CenterX=0 CenterY=2.44e-14 CenterZ=0 NormalX=0 NormalY=0 NormalZ=1 AngleXU=0 Radius=22
  constraints (1):
    c: Coincident(g0,g-3)
FEATURE [Part::Face] Face003
  FaceMakerClass = Part::FaceMakerBullseye
  Sources = -> [Sketch014]
FEATURE [Part::Extrusion] Extrude046
  Base = -> Face003
  Dir = (0,1,0)
  DirMode = 0
  FaceMakerClass = Part::FaceMakerBullseye
  LengthFwd = 3
  LengthRev = 0
  Solid = true
  Symmetric = false
FEATURE [Part::Extrusion] Extrude047
  Base = -> Face003
  Dir = (0,1,0)
  DirMode = 0
  FaceMakerClass = Part::FaceMakerBullseye
  LengthFwd = 3
  LengthRev = 0
  Solid = true
  Symmetric = false
FEATURE [Part::Cut] Cut002
  Base = -> Fusion007
  Tool = -> Extrude046
FEATURE [Sketcher::SketchObject] Sketch015
  FullyConstrained = true
  Placement = pos=(0,-110,0) rot=(1,0,0;1.5708rad)
  sketch-geometry (1):
    g0: Circle CenterX=0 CenterY=0 CenterZ=0 NormalX=0 NormalY=0 NormalZ=1 AngleXU=0 Radius=2.5
  constraints (2):
    c: Coincident(g0,g-1)
    c: Diameter(g0) = 5
FEATURE [Part::Face] Face004
  FaceMakerClass = Part::FaceMakerBullseye
  Sources = -> [Sketch015]
FEATURE [Part::Extrusion] Extrude048
  Base = -> Face004
  Dir = (0,1,0)
  DirMode = 0
  FaceMakerClass = Part::FaceMakerBullseye
  LengthFwd = 157
  LengthRev = 0
  Solid = false
  Symmetric = false
FEATURE [Sketcher::SketchObject] Sketch016
  ExternalGeometry = -> [Sketch015,Cut002]
  FullyConstrained = true
  Placement = pos=(0,47,0) rot=(1,0,0;1.5708rad)
  sketch-geometry (1):
    g0: Circle CenterX=0 CenterY=0 CenterZ=0 NormalX=0 NormalY=0 NormalZ=1 AngleXU=0 Radius=12.5
  constraints (2):
    c: Coincident(g0,g-4)
    c: Diameter(g0) = 25
FEATURE [Part::Face] Face005
  FaceMakerClass = Part::FaceMakerBullseye
  Sources = -> [Sketch016]
FEATURE [Part::Extrusion] Extrude049
  Base = -> Sketch016
  Dir = (0,-1,0)
  DirMode = 0
  FaceMakerClass = Part::FaceMakerBullseye
  LengthFwd = 30
  LengthRev = 0
  Solid = true
  Symmetric = false
FEATURE [App::LinkGroup] LinkGroup  label="inutil1"
  ElementList = -> [Line007,Line010,Line019,Line020,Line021,Line022,Line028,Line029,Line030,Line031,Line032,Line033,Line034,Line035,Line036,Line037,Line038,Line039,Line040,Line041,Line042,Line043,Line045,Line048,Line049,Line052,Line053,Line056,Line065,Line067,Line074,Line080,Line081,Line083,Line084,Line085,Line086,Line088,Line091,Line096,Line101,Line102,Line103,Line106,Line107,Line108,Line109,Line112,Line113,Line114,+1 more]
  LinkMode = 0
FEATURE [App::LinkGroup] LinkGroup001  label="inutil2"
  ElementList = -> [Line130,Line146,Line148,Line168]
  LinkMode = 0
FEATURE [Part::MultiFuse] Fusion009
  Placement = pos=(-25,-37.5,-2260) rot=(0,0,1;0rad)
  Shapes = -> [Extrude,Extrude001,Extrude002,Extrude003,Extrude004,Extrude005,Extrude006,Extrude007,Extrude008,Extrude009,Extrude010,Extrude011,Extrude012,Extrude013,Extrude014]
FEATURE [App::Link] Link  label="Sweep002"
  LinkTransform = true
  LinkedObject = -> Sweep
FEATURE [Part::Cylinder] Cylinder001  label="Cilindro001"
  Angle = 360
  AttacherType = Attacher::AttachEngine3D
  FirstAngle = 0
  Height = 20
  Placement = pos=(0,0,-535) rot=(0,0,1;0rad)
  Radius = 296
  SecondAngle = 0
FEATURE [Part::Cylinder] Cylinder002  label="Cilindro002"
  Angle = 360
  AttacherType = Attacher::AttachEngine3D
  FirstAngle = 0
  Height = 20
  Placement = pos=(0,0,-535) rot=(0,0,1;0rad)
  Radius = 290
  SecondAngle = 0
FEATURE [Part::Cut] Cut003  label="Cut004"
  Base = -> Cylinder001
  Tool = -> Cylinder002
FEATURE [Part::Box] Box  label="Cubo"
  AttacherType = Attacher::AttachEngine3D
  Height = 10
  Length = 290
  Placement = pos=(0,-5,-525) rot=(0,0,1;0rad)
  Width = 10
FEATURE [Part::FeaturePython] Array003  label="Array006"  # Draft array (typed FeaturePython)
  AlwaysSyncPlacement = false
  Angle = 360
  ArrayType = 1
  Axis = (0,0,1)
  Base = -> Box
  Center = (0,0,0)
  Count = 6
  ExpandArray = false
  Fuse = true
  IntervalAxis = (0,0,0)
  IntervalX = (50,0,0)
  IntervalY = (0,50,0)
  IntervalZ = (0,0,50)
  NumberCircles = 3
  NumberPolar = 6
  NumberX = 2
  NumberY = 2
  NumberZ = 1
  PlacementList = 6 placements: [(0,-5,-525),(4.33013,-2.5,-525),(4.33013,2.5,-525),(6.12323e-16,5,-525),(-4.33013,2.5,-525),(-4.33013,-2.5,-525)]
  RadialDistance = 50
  ScaleList = (6) [(1,1,1),(1,1,1),(1,1,1),(1,1,1),(1,1,1),(1,1,1)]
  Symmetry = 1
  TangentialDistance = 25
FEATURE [Sketcher::SketchObject] Sketch017
  FullyConstrained = true
  Placement = pos=(0,0,-540) rot=(1,0,0;3.14159rad)
  sketch-geometry (5):
    g0: LineSegment StartX=0 StartY=0 StartZ=0 EndX=0 EndY=-480 EndZ=0
    g1: Circle CenterX=0 CenterY=-480 CenterZ=0 NormalX=0 NormalY=0 NormalZ=1 AngleXU=0 Radius=12.5
    g2: Circle CenterX=0 CenterY=0 CenterZ=0 NormalX=0 NormalY=0 NormalZ=1 AngleXU=0 Radius=296
    g3: Circle CenterX=0 CenterY=0 CenterZ=0 NormalX=0 NormalY=0 NormalZ=1 AngleXU=0 Radius=298
    g4: Circle CenterX=0 CenterY=-480 CenterZ=0 NormalX=0 NormalY=0 NormalZ=1 AngleXU=0 Radius=14.5
  constraints (11):
    c: Coincident(g0,g-1)
    c: Vertical(g0)
    c: DistanceY(g0,g0) = 480
    c: Coincident(g1,g0)
    c: Diameter(g1) = 25
    c: Coincident(g2,g0)
    c: Diameter(g2) = 592
    c: Coincident(g3,g0)
    c: Diameter(g3) = 596
    c: Coincident(g4,g0)
    c: Diameter(g4) = 29
FEATURE [Sketcher::SketchObject] Sketch018
  ExternalGeometry = -> [Sketch017,Cut003]
  FullyConstrained = true
  Placement = pos=(0,0,-535) rot=(1,0,0;3.14159rad)
  sketch-geometry (8):
    g0: LineSegment StartX=10.0868 StartY=-487.383 StartZ=0 EndX=238.856 EndY=-174.825 EndZ=0
    g1: LineSegment StartX=-238.856 StartY=-174.825 StartZ=0 EndX=-10.0868 EndY=-487.383 EndZ=0
    g2: ArcOfCircle CenterX=-1.77e-14 CenterY=6e-16 CenterZ=0 NormalX=0 NormalY=0 NormalZ=1 AngleXU=0 Radius=296 StartAngle=5.65135 EndAngle=10.0566
    g3: ArcOfCircle CenterX=0 CenterY=-480 CenterZ=0 NormalX=0 NormalY=0 NormalZ=1 AngleXU=0 Radius=12.5 StartAngle=3.77343 EndAngle=5.65135
    g4: LineSegment StartX=240.47 StartY=-176.006 StartZ=0 EndX=11.7007 EndY=-488.564 EndZ=0
    g5: LineSegment StartX=-11.7007 StartY=-488.564 StartZ=0 EndX=-240.47 EndY=-176.006 EndZ=0
    g6: ArcOfCircle CenterX=0 CenterY=-480 CenterZ=0 NormalX=0 NormalY=0 NormalZ=1 AngleXU=0 Radius=14.5 StartAngle=3.77343 EndAngle=5.65135
    g7: ArcOfCircle CenterX=-1.77e-14 CenterY=6e-16 CenterZ=0 NormalX=0 NormalY=0 NormalZ=1 AngleXU=0 Radius=298 StartAngle=5.65135 EndAngle=10.0566
  constraints (22):
    c: Tangent(g0,g-3) = -1.5708
    c: Tangent(g0,g-5) = -1.5708
    c: Tangent(g1,g-5) = -1.5708
    c: Tangent(g1,g-3) = -1.5708
    c: Coincident(g2,g-5)
    c: Diameter(g2) = 592
    c: Horizontal(g2,g0)
    c: Horizontal(g2,g1)
    c: Coincident(g3,g-3)
    c: Diameter(g3) = 25
    c: Horizontal(g3,g1)
    c: Horizontal(g3,g0)
    c: Tangent(g5,g-6) = 1.5708
    c: Tangent(g5,g-7) = 1.5708
    c: Tangent(g4,g-7) = 1.5708
    c: Tangent(g4,g-6) = 1.5708
    c: Coincident(g6,g3)
    c: Coincident(g6,g5)
    c: Coincident(g6,g4)
    c: Coincident(g7,g2)
    c: Coincident(g7,g5)
    c: Coincident(g7,g4)
FEATURE [Part::Face] Face006
  FaceMakerClass = Part::FaceMakerBullseye
  Sources = -> [Sketch018]
FEATURE [Sketcher::SketchObject] Sketch019
  FullyConstrained = true
  Placement = pos=(0,0,-495) rot=(1,0,0;3.14159rad)
  sketch-geometry (4):
    g0: GeomPoint X=72 Y=-535 Z=0
    g1: Circle CenterX=72 CenterY=-535 CenterZ=0 NormalX=0 NormalY=0 NormalZ=1 AngleXU=0 Radius=10
    g2: GeomPoint X=-72 Y=-535 Z=0
    g3: Circle CenterX=-72 CenterY=-535 CenterZ=0 NormalX=0 NormalY=0 NormalZ=1 AngleXU=0 Radius=10
  constraints (8):
    c: DistanceY(g0,g-1) = 535
    c: DistanceX(g-1,g0) = 72
    c: Coincident(g1,g0)
    c: Diameter(g1) = 20
    c: Horizontal(g1,g2)
    c: DistanceX(g2,g1) = 144
    c: Coincident(g3,g2)
    c: Diameter(g3) = 20
FEATURE [Part::Face] Face007
  FaceMakerClass = Part::FaceMakerBullseye
  Sources = -> [Sketch019]
FEATURE [Part::Extrusion] Extrude051  label="Extrude053"
  Base = -> Face007
  Dir = (0,0,1)
  DirMode = 2
  FaceMakerClass = Part::FaceMakerBullseye
  LengthFwd = 270
  LengthRev = 0
  Solid = true
  Symmetric = false
FEATURE [Sketcher::SketchObject] Sketch020
  FullyConstrained = true
  Placement = pos=(0,0,0) rot=(0.57735,0.57735,0.57735;2.0944rad)
  sketch-geometry (5):
    g0: GeomPoint X=535 Y=-232 Z=0
    g1: LineSegment StartX=510 StartY=-207 StartZ=0 EndX=560 EndY=-207 EndZ=0
    g2: LineSegment StartX=560 StartY=-207 StartZ=0 EndX=560 EndY=-257 EndZ=0
    g3: LineSegment StartX=560 StartY=-257 StartZ=0 EndX=510 EndY=-257 EndZ=0
    g4: LineSegment StartX=510 StartY=-257 StartZ=0 EndX=510 EndY=-207 EndZ=0
  constraints (15):
    c: DistanceY(g0,g-1) = 232
    c: DistanceX(g-1,g0) = 535
    c: Horizontal(g1)
    c: Vertical(g2)
    c: Horizontal(g3)
    c: Vertical(g4)
    c: DistanceY(g4,g0) = 25
    c: DistanceX(g4,g0) = 25
    c: Distance(g4,g4) = 50
    c: Coincident(g3,g4)
    c: Coincident(g1,g4)
    c: Distance(g1,g1) = 50
    c: Distance(g3,g3) = 50
    c: Distance(g2,g2) = 50
    c: Coincident(g3,g2)
FEATURE [Part::Face] Face008
  FaceMakerClass = Part::FaceMakerBullseye
  Sources = -> [Sketch020]
FEATURE [Part::Extrusion] Extrude052  label="Extrude054"
  Base = -> Face008
  Dir = (1,0,0)
  DirMode = 2
  FaceMakerClass = Part::FaceMakerBullseye
  LengthFwd = 200
  LengthRev = 0
  Solid = true
  Symmetric = true
FEATURE [Part::FeaturePython] Array004  label="Array007"  # Draft array (typed FeaturePython)
  AlwaysSyncPlacement = false
  Angle = 360
  ArrayType = 1
  Axis = (0,0,1)
  Base = -> Sweep001
  Center = (0,0,0)
  Count = 3
  ExpandArray = false
  Fuse = true
  IntervalAxis = (0,0,0)
  IntervalX = (50,0,0)
  IntervalY = (0,50,0)
  IntervalZ = (0,0,50)
  NumberCircles = 3
  NumberPolar = 3
  NumberX = 2
  NumberY = 2
  NumberZ = 1
  PlacementList = 3 placements: [(0,0,0),(0,0,0),(0,0,0)]
  RadialDistance = 50
  ScaleList = (3) [(1,1,1),(1,1,1),(1,1,1)]
  Symmetry = 1
  TangentialDistance = 25
FEATURE [Part::Feature] Fillet_solid  label="aleta 1"
  shape: bbox 774.6 x 621.5 x 905.9 mm, 7 faces (baked)
FEATURE [Part::FeaturePython] Clone  label="aleta2"  # Draft clone (typed FeaturePython)
  AttacherType = Attacher::AttachEngine3D
  Fuse = false
  Objects = -> [Fillet_solid]
  Placement = pos=(0,0,0) rot=(0,0,1;2.0944rad)
  Scale = (1,1,1)
FEATURE [Part::FeaturePython] Clone001  label="aleta3"  # Draft clone (typed FeaturePython)
  AttacherType = Attacher::AttachEngine3D
  Fuse = false
  Objects = -> [Clone]
  Placement = pos=(0,0,0) rot=(0,0,1;4.18879rad)
  Scale = (1,1,1)
FEATURE [Part::MultiFuse] Fusion011  label="Fusion013"
  Shapes = -> [Fusion009,Extrude051,Extrude052]
FEATURE [App::Link] Link003  label="Array005"
  LinkTransform = true
FEATURE [App::LinkGroup] LinkGroup002
  ElementList = -> [Link,Link003]
  LinkMode = 1
FEATURE [App::Link] Link004  label="Extrude050"
  LinkTransform = true
  LinkedObject = -> Extrude049
FEATURE [App::Link] Link005  label="Extrude051"
  LinkTransform = true
  LinkedObject = -> Extrude048
FEATURE [App::Link] Link006  label="Cut003"
  LinkTransform = true
  LinkedObject = -> Cut002
FEATURE [App::Link] Link007  label="Fusion010"
  LinkTransform = true
  LinkedObject = -> Fusion006
FEATURE [App::Link] Link008  label="Fusion011"
  LinkTransform = true
  LinkedObject = -> Fusion005
FEATURE [Part::MultiFuse] Fusion012  label="Fusion014"
  Placement = pos=(0,480,-490) rot=(0,-0.707107,0.707107;3.14159rad)
  Shapes = -> [Link004,Link005,Link006,Link007,Link008]
FEATURE [App::LinkGroup] LinkGroup003
  ElementList = -> [Link004,Link005,Link006,Link007,Link008]
  LinkMode = 1
  Placement = pos=(0,480,-490) rot=(0,0.707107,-0.707107;3.14159rad)
FEATURE [Part::Feature] Fusion010_solid  label="ALAMBRES"
  shape: bbox 743.2 x 856.7 x 1000 mm, 17 faces (baked)
FEATURE [Part::Feature] Fusion011_solid  label="estructura"
  shape: bbox 200 x 748.2 x 1100 mm, 78 faces (baked)
FEATURE [Part::Feature] Fusion012_solid  label="motor"
  shape: bbox 176.3 x 127.5 x 232 mm, 223 faces (baked)
FEATURE [Part::MultiFuse] Fusion013  label="Fusion015"
  Shapes = -> [Array003,Cut003]
FEATURE [Part::Feature] Fusion013_solid  label="Polea"
  shape: bbox 592 x 592 x 20 mm, 30 faces (baked)
FEATURE [Part::Extrusion] Extrude050  label="Correa"
  Base = -> Face006
  Dir = (0,0,1)
  DirMode = 0
  FaceMakerClass = Part::FaceMakerBullseye
  LengthFwd = 20
  LengthRev = 0
  Solid = true
  Symmetric = false
FEATURE [Part::FeaturePython] Array005  label="Array008"  # Draft array (typed FeaturePython)
  AlwaysSyncPlacement = false
  Angle = 360
  ArrayType = 1
  Axis = (0,0,1)
  Base = -> Extrude050
  Center = (0,0,0)
  Count = 3
  ExpandArray = false
  Fuse = true
  IntervalAxis = (0,0,0)
  IntervalX = (50,0,0)
  IntervalY = (0,50,0)
  IntervalZ = (0,0,50)
  NumberCircles = 3
  NumberPolar = 3
  NumberX = 2
  NumberY = 2
  NumberZ = 1
  PlacementList = 3 placements: [(0,0,0),(0,0,0),(0,0,0)]
  RadialDistance = 50
  ScaleList = (3) [(1,1,1),(1,1,1),(1,1,1)]
  Symmetry = 1
  TangentialDistance = 25
FEATURE [Part::MultiFuse] Fusion010  label="Fusion012"
  Shapes = -> [Array005,Array004]
FEATURE [App::LinkGroup] LinkGroup004
  ElementList = -> [Fusion012_solid,Fusion011_solid,Fusion010_solid,Fusion012,Clone001,Clone,Fillet_solid,Fusion013_solid,Extrude050]
  LinkMode = 0
FEATURE [Mesh::Feature] Mesh  label="motor (Meshed)"
FEATURE [Mesh::Feature] Mesh001  label="estructura (Meshed)"
FEATURE [Mesh::Feature] Mesh002  label="ALAMBRES (Meshed)"
FEATURE [Mesh::Feature] Mesh003  label="Fusion014 (Meshed)"
FEATURE [Mesh::Feature] Mesh004  label="aleta3 (Meshed)"
FEATURE [Mesh::Feature] Mesh005  label="aleta2 (Meshed)"
FEATURE [Mesh::Feature] Mesh006  label="aleta 1 (Meshed)"
FEATURE [Mesh::Feature] Mesh007  label="Polea (Meshed)"
FEATURE [Mesh::Feature] Mesh008  label="Correa (Meshed)"
